# Revit family: CA-4_SWSI_ARR_1_CW_DBD
name_source: partatom
category: Mechanical Equipment
units: mm (PartAtom-declared; Revit-internal decimal feet)

## family parameters
Always vertical = Yes
Cut with Voids When Loaded = No
Part Type = Normal
Room Calculation Point = No
Round Connector Dimension = Use Radius
Shared = No
Work Plane-Based = No

## types (54) — shared parameters
0 = 0"
1" = 1"
1.5 = 1 1/2"
2" = 2"
2' = 24"
3" = 3"
4" = 4"
Manufacturer = Loren Cook Company
ONE EIGTH = 1/8"
Type Comments = Airfoil Centrifugal Blower Arrangement 1 Clockwise Down Blast Discharge
URL = www.lorencook.com

## per-type parameters (varying)
- 120_CA-4_SWSI_ARR_1_CW_DBD_CLASS_1: ((D-B)/2)-.125"=1 7/8"; ((K-B)/2)+B=12 17/32"; (D-B)/2=2"; (R-B)/2=1 1/8"; -(((D - B) / 2) - 1/8")=-1 7/8"; -(((K-B)/2)+L)=-6 11/32"; -(((K-B)/2)-.125")=-3 7/32"; -(ARR_2_L - ARR_2_K)=-17 5/8"; -ARR_1_J=-1 3/16"; 2ARR_1_J=2 3/8"; 2ARR_1_J+1"=3 3/8"; A=13 1/8"; ARR_1_G=9 3/16"; ARR_1_H=8 7/16"; ARR_1_J=1 3/16"; ARR_1_J/2=19/32"; ARR_1_K=30 13/16"; ARR_1_K-D=17 5/8"; ARR_1_M=1"; ARR_1_N=15 1/8"; ARR_1_U=34 13/16"; ARR_1_U-D=21 5/8"; ARR_1_V=4"; ARR_2_K=4"; ARR_2_L=21 5/8"; ARR_2_L-ARR_2_K=17 5/8"; B=9 3/16"; D=13 3/16"; D-((D-B)/2)=11 3/16"; E=10 3/4"; E+(INLET_RAD+1.5")=20"; E-(INLET_RAD+1.5")=3/4"; F=25 3/4"; F-E=15"; F/5=5 5/32"; G=22 3/4"; H=10 3/8"; INLET_DIA=16 1/4"; INLET_RAD=8 1/8"; INLET_RAD+1.5"=9 5/8"; INLET_RAD/2=4 1/16"; J=2"; K=15 7/8"; L=3"; M=18 7/8"; MOTOR_RAD=3 9/16"; Model=CA-4 SWSI ARR 1 CW DBD CLASS 1; O=11/16"; O/2=11/32"; P=5 23/32"; R=11 7/16"; S=7 1/2"
- 135_CA-4_SWSI_ARR_1_CW_DBD_CLASS_1: ((D-B)/2)-.125"=1 7/8"; ((K-B)/2)+B=13 21/32"; (D-B)/2=2"; (R-B)/2=1 1/8"; -(((D - B) / 2) - 1/8")=-1 7/8"; -(((K-B)/2)+L)=-6 11/32"; -(((K-B)/2)-.125")=-3 7/32"; -(ARR_2_L - ARR_2_K)=-17 5/8"; -ARR_1_J=-1 3/16"; 2ARR_1_J=2 3/8"; 2ARR_1_J+1"=3 3/8"; A=14 3/4"; ARR_1_G=9 15/16"; ARR_1_H=9 3/16"; ARR_1_J=1 3/16"; ARR_1_J/2=19/32"; ARR_1_K=31 15/16"; ARR_1_K-D=17 5/8"; ARR_1_M=1"; ARR_1_N=15 1/8"; ARR_1_U=35 15/16"; ARR_1_U-D=21 5/8"; ARR_1_V=4"; ARR_2_K=4"; ARR_2_L=21 5/8"; ARR_2_L-ARR_2_K=17 5/8"; B=10 5/16"; D=14 5/16"; D-((D-B)/2)=12 5/16"; E=12"; E+(INLET_RAD+1.5")=22"; E-(INLET_RAD+1.5")=1 1/4"; F=28 3/4"; F-E=16 3/4"; F/5=5 3/4"; G=25 1/2"; H=11 5/8"; INLET_DIA=17 3/4"; INLET_RAD=8 7/8"; INLET_RAD+1.5"=10 3/8"; INLET_RAD/2=4 7/16"; J=2"; K=17"; L=3"; M=20"; MOTOR_RAD=3 9/16"; Model=CA-4 SWSI ARR 1 CW DBD CLASS 1; O=11/16"; O/2=11/32"; P=6 9/32"; R=12 9/16"; S=8 1/2"
- 150_CA-4_SWSI_ARR_1_CW_DBD_CLASS_1: ((D-B)/2)-.125"=1 7/8"; ((K-B)/2)+B=14 25/32"; (D-B)/2=2"; (R-B)/2=1 1/8"; -(((D - B) / 2) - 1/8")=-1 7/8"; -(((K-B)/2)+L)=-6 11/32"; -(((K-B)/2)-.125")=-3 7/32"; -(ARR_2_L - ARR_2_K)=-17 5/8"; -ARR_1_J=-1 3/16"; 2ARR_1_J=2 3/8"; 2ARR_1_J+1"=3 3/8"; A=16 7/16"; ARR_1_G=10 11/16"; ARR_1_H=9 15/16"; ARR_1_J=1 3/16"; ARR_1_J/2=19/32"; ARR_1_K=33 1/16"; ARR_1_K-D=17 5/8"; ARR_1_M=1"; ARR_1_N=15 1/8"; ARR_1_U=37 1/16"; ARR_1_U-D=21 5/8"; ARR_1_V=4"; ARR_2_K=4"; ARR_2_L=21 5/8"; ARR_2_L-ARR_2_K=17 5/8"; B=11 7/16"; D=15 7/16"; D-((D-B)/2)=13 7/16"; E=13 1/4"; E+(INLET_RAD+1.5")=24"; E-(INLET_RAD+1.5")=1 3/4"; F=31 5/8"; F-E=18 3/8"; F/5=6 5/16"; G=28 1/8"; H=12 7/8"; INLET_DIA=19 1/4"; INLET_RAD=9 5/8"; INLET_RAD+1.5"=11 1/8"; INLET_RAD/2=4 13/16"; J=2"; K=18 1/8"; L=3"; M=21 1/8"; MOTOR_RAD=3 9/16"; Model=CA-4 SWSI ARR 1 CW DBD CLASS 1; O=11/16"; O/2=11/32"; P=6 27/32"; R=13 11/16"; S=9"
- 165_CA-4_SWSI_ARR_1_CW_DBD_CLASS_1: ((D-B)/2)-.125"=1 7/8"; ((K-B)/2)+B=15 31/32"; (D-B)/2=2"; (R-B)/2=1 1/8"; -(((D - B) / 2) - 1/8")=-1 7/8"; -(((K-B)/2)+L)=-7 11/32"; -(((K-B)/2)-.125")=-3 7/32"; -(ARR_2_L - ARR_2_K)=-17 5/8"; -ARR_1_J=-1 3/16"; 2ARR_1_J=2 3/8"; 2ARR_1_J+1"=3 3/8"; A=18 1/16"; ARR_1_G=11 11/16"; ARR_1_H=10 15/16"; ARR_1_J=1 3/16"; ARR_1_J/2=19/32"; ARR_1_K=34 1/4"; ARR_1_K-D=17 5/8"; ARR_1_M=1"; ARR_1_N=15 1/8"; ARR_1_U=38 1/4"; ARR_1_U-D=21 5/8"; ARR_1_V=4"; ARR_2_K=4"; ARR_2_L=21 5/8"; ARR_2_L-ARR_2_K=17 5/8"; B=12 5/8"; D=16 5/8"; D-((D-B)/2)=14 5/8"; E=14 3/8"; E+(INLET_RAD+1.5")=26 3/8"; E-(INLET_RAD+1.5")=2 1/8"; F=34 3/8"; F-E=20"; F/5=6 7/8"; G=30 7/8"; H=14 1/4"; INLET_DIA=21 1/4"; INLET_RAD=10 5/8"; INLET_RAD+1.5"=12 1/8"; INLET_RAD/2=5 5/16"; J=2"; K=19 5/16"; L=4"; M=23 15/16"; MOTOR_RAD=3 9/16"; Model=CA-4 SWSI ARR 1 CW DBD CLASS 1; O=11/16"; O/2=11/32"; P=7 7/16"; R=14 7/8"; S=10"
- 180_CA-4_SWSI_ARR_1_CW_DBD_CLASS_1: ((D-B)/2)-.125"=1 7/8"; ((K-B)/2)+B=17 3/32"; (D-B)/2=2"; (R-B)/2=1 1/8"; -(((D - B) / 2) - 1/8")=-1 7/8"; -(((K-B)/2)+L)=-7 27/32"; -(((K-B)/2)-.125")=-3 7/32"; -(ARR_2_L - ARR_2_K)=-20 1/8"; -ARR_1_J=-1 3/16"; 2ARR_1_J=2 3/8"; 2ARR_1_J+1"=3 3/8"; A=19 11/16"; ARR_1_G=12 7/16"; ARR_1_H=11 11/16"; ARR_1_J=1 3/16"; ARR_1_J/2=19/32"; ARR_1_K=37 7/8"; ARR_1_K-D=20 1/8"; ARR_1_M=1"; ARR_1_N=17 5/8"; ARR_1_U=42 1/8"; ARR_1_U-D=24 3/8"; ARR_1_V=4 1/4"; ARR_2_K=4 1/4"; ARR_2_L=24 3/8"; ARR_2_L-ARR_2_K=20 1/8"; B=13 3/4"; D=17 3/4"; D-((D-B)/2)=15 3/4"; E=15 5/8"; E+(INLET_RAD+1.5")=28 3/8"; E-(INLET_RAD+1.5")=2 5/8"; F=37 1/8"; F-E=21 1/2"; F/5=7 7/16"; G=33 5/8"; H=15 1/2"; INLET_DIA=22 3/4"; INLET_RAD=11 3/8"; INLET_RAD+1.5"=12 7/8"; INLET_RAD/2=5 11/16"; J=2"; K=20 7/16"; L=4 1/2"; M=24 15/16"; MOTOR_RAD=3 9/16"; Model=CA-4 SWSI ARR 1 CW DBD CLASS 1; O=11/16"; O/2=11/32"; P=8"; R=16"; S=11"
- 195_CA-4_SWSI_ARR_1_CW_DBD_CLASS_1: ((D-B)/2)-.125"=1 7/8"; ((K-B)/2)+B=18 13/16"; (D-B)/2=2"; (R-B)/2=1 1/8"; -(((D - B) / 2) - 1/8")=-1 7/8"; -(((K-B)/2)+L)=-8 3/8"; -(((K-B)/2)-.125")=-3 3/4"; -(ARR_2_L - ARR_2_K)=-20 1/8"; -ARR_1_J=-1 3/16"; 2ARR_1_J=2 3/8"; 2ARR_1_J+1"=3 3/8"; A=21 5/16"; ARR_1_G=13 3/16"; ARR_1_H=12 7/16"; ARR_1_J=1 3/16"; ARR_1_J/2=19/32"; ARR_1_K=39 1/16"; ARR_1_K-D=20 1/8"; ARR_1_M=1"; ARR_1_N=17 5/8"; ARR_1_U=43 5/16"; ARR_1_U-D=24 3/8"; ARR_1_V=4 1/4"; ARR_2_K=4 1/4"; ARR_2_L=24 3/8"; ARR_2_L-ARR_2_K=20 1/8"; B=14 15/16"; D=18 15/16"; D-((D-B)/2)=16 15/16"; E=16 3/4"; E+(INLET_RAD+1.5")=30 3/8"; E-(INLET_RAD+1.5")=3 1/8"; F=40"; F-E=23 1/4"; F/5=8"; G=36 1/4"; H=16 3/4"; INLET_DIA=24 1/4"; INLET_RAD=12 1/8"; INLET_RAD+1.5"=13 5/8"; INLET_RAD/2=6 1/16"; J=2"; K=22 11/16"; L=4 1/2"; M=27 3/16"; MOTOR_RAD=3 9/16"; Model=CA-4 SWSI ARR 1 CW DBD CLASS 1; O=11/16"; O/2=11/32"; P=8 19/32"; R=17 3/16"; S=11 1/2"
- 210_CA-4_SWSI_ARR_1_CW_DBD_CLASS_1: ((D-B)/2)-.125"=1 7/8"; ((K-B)/2)+B=19 15/16"; (D-B)/2=2"; (R-B)/2=1 1/8"; -(((D - B) / 2) - 1/8")=-1 7/8"; -(((K-B)/2)+L)=-8 7/8"; -(((K-B)/2)-.125")=-3 3/4"; -(ARR_2_L - ARR_2_K)=-23 1/8"; -ARR_1_J=-1 7/16"; 2ARR_1_J=2 7/8"; 2ARR_1_J+1"=3 7/8"; A=23"; ARR_1_G=14 1/16"; ARR_1_H=13 5/16"; ARR_1_J=1 7/16"; ARR_1_J/2=23/32"; ARR_1_K=42 3/16"; ARR_1_K-D=22 1/8"; ARR_1_M=1"; ARR_1_N=19 9/16"; ARR_1_U=46 7/16"; ARR_1_U-D=26 3/8"; ARR_1_V=4 1/4"; ARR_2_K=4 1/4"; ARR_2_L=27 3/8"; ARR_2_L-ARR_2_K=23 1/8"; B=16 1/16"; D=20 1/16"; D-((D-B)/2)=18 1/16"; E=18"; E+(INLET_RAD+1.5")=32 5/8"; E-(INLET_RAD+1.5")=3 5/8"; F=42 7/8"; F-E=24 7/8"; F/5=8 9/16"; G=39 1/8"; H=18 1/8"; INLET_DIA=26"; INLET_RAD=13"; INLET_RAD+1.5"=14 1/2"; INLET_RAD/2=6 1/2"; J=2"; K=23 13/16"; L=5"; M=28 13/16"; MOTOR_RAD=4 5/16"; Model=CA-4 SWSI ARR 1 CW DBD CLASS 1; O=13/16"; O/2=13/32"; P=9 5/32"; R=18 5/16"; S=12"
- 225_CA-4_SWSI_ARR_1_CW_DBD_CLASS_1: ((D-B)/2)-.125"=1 7/8"; ((K-B)/2)+B=21 1/16"; (D-B)/2=2"; (R-B)/2=1 1/8"; -(((D - B) / 2) - 1/8")=-1 7/8"; -(((K-B)/2)+L)=-8 7/8"; -(((K-B)/2)-.125")=-3 3/4"; -(ARR_2_L - ARR_2_K)=-23 1/8"; -ARR_1_J=-1 7/16"; 2ARR_1_J=2 7/8"; 2ARR_1_J+1"=3 7/8"; A=24 5/8"; ARR_1_G=14 13/16"; ARR_1_H=14 1/16"; ARR_1_J=1 7/16"; ARR_1_J/2=23/32"; ARR_1_K=43 5/16"; ARR_1_K-D=22 1/8"; ARR_1_M=1"; ARR_1_N=19 9/16"; ARR_1_U=47 9/16"; ARR_1_U-D=26 3/8"; ARR_1_V=4 1/4"; ARR_2_K=4 1/4"; ARR_2_L=27 3/8"; ARR_2_L-ARR_2_K=23 1/8"; B=17 3/16"; D=21 3/16"; D-((D-B)/2)=19 3/16"; E=19 1/4"; E+(INLET_RAD+1.5")=34 5/8"; E-(INLET_RAD+1.5")=4 1/8"; F=45 3/4"; F-E=26 1/2"; F/5=9 5/32"; G=41 3/4"; H=19 3/8"; INLET_DIA=27 1/2"; INLET_RAD=13 3/4"; INLET_RAD+1.5"=15 1/4"; INLET_RAD/2=6 7/8"; J=2"; K=24 15/16"; L=5"; M=29 15/16"; MOTOR_RAD=4 5/16"; Model=CA-4 SWSI ARR 1 CW DBD CLASS 1; O=13/16"; O/2=13/32"; P=9 23/32"; R=19 7/16"; S=12 1/2"
- 245_CA-4_SWSI_ARR_1_CW_DBD_CLASS_1: ((D-B)/2)-.125"=1 7/8"; ((K-B)/2)+B=22 5/8"; (D-B)/2=2"; (R-B)/2=1 1/8"; -(((D - B) / 2) - 1/8")=-1 7/8"; -(((K-B)/2)+L)=-9 3/8"; -(((K-B)/2)-.125")=-3 3/4"; -(ARR_2_L - ARR_2_K)=-22 9/16"; -ARR_1_J=-1 11/16"; 2ARR_1_J=3 3/8"; 2ARR_1_J+1"=4 3/8"; A=26 13/16"; ARR_1_G=15 13/16"; ARR_1_H=15 1/16"; ARR_1_J=1 11/16"; ARR_1_J/2=27/32"; ARR_1_K=45 3/8"; ARR_1_K-D=22 5/8"; ARR_1_M=1"; ARR_1_N=20 1/8"; ARR_1_U=50 9/16"; ARR_1_U-D=27 13/16"; ARR_1_V=5 1/4"; ARR_2_K=5 1/4"; ARR_2_L=27 13/16"; ARR_2_L-ARR_2_K=22 9/16"; B=18 3/4"; D=22 3/4"; D-((D-B)/2)=20 3/4"; E=20 7/8"; E+(INLET_RAD+1.5")=37 3/8"; E-(INLET_RAD+1.5")=4 7/8"; F=49 1/2"; F-E=28 5/8"; F/5=9 29/32"; G=45 3/8"; H=21 1/8"; INLET_DIA=29 1/2"; INLET_RAD=14 3/4"; INLET_RAD+1.5"=16 1/4"; INLET_RAD/2=7 3/8"; J=2"; K=26 1/2"; L=5 1/2"; M=32"; MOTOR_RAD=5 1/16"; Model=CA-4 SWSI ARR 1 CW DBD CLASS 1; O=13/16"; O/2=13/32"; P=10 1/2"; R=21"; S=13 1/2"
- 270_CA-4_SWSI_ARR_1_CW_DBD_CLASS_1: ((D-B)/2)-.125"=1 7/8"; ((K-B)/2)+B=24 1/2"; (D-B)/2=2"; (R-B)/2=1 1/8"; -(((D - B) / 2) - 1/8")=-1 7/8"; -(((K-B)/2)+L)=-9 7/8"; -(((K-B)/2)-.125")=-3 3/4"; -(ARR_2_L - ARR_2_K)=-22 9/16"; -ARR_1_J=-1 11/16"; 2ARR_1_J=3 3/8"; 2ARR_1_J+1"=4 3/8"; A=29 9/16"; ARR_1_G=17 3/16"; ARR_1_H=16 7/16"; ARR_1_J=1 11/16"; ARR_1_J/2=27/32"; ARR_1_K=47 1/4"; ARR_1_K-D=22 5/8"; ARR_1_M=1"; ARR_1_N=20 1/8"; ARR_1_U=52 7/16"; ARR_1_U-D=27 13/16"; ARR_1_V=5 1/4"; ARR_2_K=5 1/4"; ARR_2_L=27 13/16"; ARR_2_L-ARR_2_K=22 9/16"; B=20 5/8"; D=24 5/8"; D-((D-B)/2)=22 5/8"; E=23 3/8"; E+(INLET_RAD+1.5")=40 3/4"; E-(INLET_RAD+1.5")=5 3/4"; F=54 3/4"; F-E=31 3/8"; F/5=10 15/16"; G=49 7/8"; H=23 1/4"; INLET_DIA=32"; INLET_RAD=16"; INLET_RAD+1.5"=17 1/2"; INLET_RAD/2=8"; J=2"; K=28 3/8"; L=6"; M=34 3/8"; MOTOR_RAD=5 1/16"; Model=CA-4 SWSI ARR 1 CW DBD CLASS 1; O=13/16"; O/2=13/32"; P=11 7/16"; R=22 7/8"; S=15"
- 300_CA-4_SWSI_ARR_1_CW_DBD_CLASS_1: ((D-B)/2)-.125"=1 7/8"; ((K-B)/2)+B=26 13/16"; (D-B)/2=2"; (R-B)/2=1 1/8"; -(((D - B) / 2) - 1/8")=-1 7/8"; -(((K-B)/2)+L)=-10 3/8"; -(((K-B)/2)-.125")=-3 3/4"; -(ARR_2_L - ARR_2_K)=-24 7/8"; -ARR_1_J=-1 15/16"; 2ARR_1_J=3 7/8"; 2ARR_1_J+1"=4 7/8"; A=32 13/16"; ARR_1_G=18 11/16"; ARR_1_H=17 15/16"; ARR_1_J=1 15/16"; ARR_1_J/2=31/32"; ARR_1_K=51 13/16"; ARR_1_K-D=24 7/8"; ARR_1_M=1"; ARR_1_N=22 3/8"; ARR_1_U=57 11/16"; ARR_1_U-D=30 3/4"; ARR_1_V=5 7/8"; ARR_2_K=5 7/8"; ARR_2_L=30 3/4"; ARR_2_L-ARR_2_K=24 7/8"; B=22 15/16"; D=26 15/16"; D-((D-B)/2)=24 15/16"; E=25 3/8"; E+(INLET_RAD+1.5")=44 7/8"; E-(INLET_RAD+1.5")=6 7/8"; F=60"; F-E=34 5/8"; F/5=12"; G=55 3/8"; H=25 7/8"; INLET_DIA=35"; INLET_RAD=17 1/2"; INLET_RAD+1.5"=19"; INLET_RAD/2=8 3/4"; J=2"; K=30 11/16"; L=6 1/2"; M=37 3/16"; MOTOR_RAD=5 13/16"; Model=CA-4 SWSI ARR 1 CW DBD CLASS 1; O=13/16"; O/2=13/32"; P=12 19/32"; R=25 3/16"; S=16 1/2"
- 330_CA-4_SWSI_ARR_1_CW_DBD_CLASS_1: ((D-B)/2)-.125"=1 7/8"; ((K-B)/2)+B=29 1/8"; (D-B)/2=2"; (R-B)/2=1 1/8"; -(((D - B) / 2) - 1/8")=-1 7/8"; -(((K-B)/2)+L)=-10 7/8"; -(((K-B)/2)-.125")=-3 3/4"; -(ARR_2_L - ARR_2_K)=-24 7/8"; -ARR_1_J=-1 15/16"; 2ARR_1_J=3 7/8"; 2ARR_1_J+1"=4 7/8"; A=36 1/8"; ARR_1_G=20 3/16"; ARR_1_H=19 7/16"; ARR_1_J=1 15/16"; ARR_1_J/2=31/32"; ARR_1_K=54 1/8"; ARR_1_K-D=24 7/8"; ARR_1_M=1"; ARR_1_N=22 3/8"; ARR_1_U=60"; ARR_1_U-D=30 3/4"; ARR_1_V=5 7/8"; ARR_2_K=5 7/8"; ARR_2_L=30 3/4"; ARR_2_L-ARR_2_K=24 7/8"; B=25 1/4"; D=29 1/4"; D-((D-B)/2)=27 1/4"; E=27 7/8"; E+(INLET_RAD+1.5")=48 7/8"; E-(INLET_RAD+1.5")=7 7/8"; F=65 3/4"; F-E=37 7/8"; F/5=13 5/32"; G=60 3/4"; H=28 3/8"; INLET_DIA=38"; INLET_RAD=19"; INLET_RAD+1.5"=20 1/2"; INLET_RAD/2=9 1/2"; J=2"; K=33"; L=7"; M=40"; MOTOR_RAD=5 13/16"; Model=CA-4 SWSI ARR 1 CW DBD CLASS 1; O=13/16"; O/2=13/32"; P=13 3/4"; R=27 1/2"; S=18"
- 365_CA-4_SWSI_ARR_1_CW_DBD_CLASS_1: ((D-B)/2)-.125"=1 7/8"; ((K-B)/2)+B=31 3/4"; (D-B)/2=2"; (R-B)/2=1 1/8"; -(((D - B) / 2) - 1/8")=-1 7/8"; -(((K-B)/2)+L)=-11 3/8"; -(((K-B)/2)-.125")=-3 3/4"; -(ARR_2_L - ARR_2_K)=-27 1/8"; -ARR_1_J=-2 3/16"; 2ARR_1_J=4 3/8"; 2ARR_1_J+1"=5 3/8"; A=39 15/16"; ARR_1_G=22 7/16"; ARR_1_H=21 11/16"; ARR_1_J=2 3/16"; ARR_1_J/2=1 3/32"; ARR_1_K=59"; ARR_1_K-D=27 1/8"; ARR_1_M=1"; ARR_1_N=24 5/8"; ARR_1_U=64 7/8"; ARR_1_U-D=33"; ARR_1_V=5 7/8"; ARR_2_K=5 7/8"; ARR_2_L=33"; ARR_2_L-ARR_2_K=27 1/8"; B=27 7/8"; D=31 7/8"; D-((D-B)/2)=29 7/8"; E=30 5/8"; E+(INLET_RAD+1.5")=53 5/8"; E-(INLET_RAD+1.5")=9 1/8"; F=72 3/8"; F-E=41 3/4"; F/5=14 15/32"; G=67"; H=31 3/8"; INLET_DIA=41 1/2"; INLET_RAD=20 3/4"; INLET_RAD+1.5"=22 1/4"; INLET_RAD/2=10 3/8"; J=2"; K=35 5/8"; L=7 1/2"; M=43 1/8"; MOTOR_RAD=6 9/16"; Model=CA-4 SWSI ARR 1 CW DBD CLASS 1; O=13/16"; O/2=13/32"; P=15 1/16"; R=30 1/8"; S=20"
- 402_CA-4_SWSI_ARR_1_CW_DBD_CLASS_1: ((D-B)/2)-.125"=2 7/8"; ((K-B)/2)+B=34 11/16"; (D-B)/2=3"; (R-B)/2=1 3/4"; -(((D - B) / 2) - 1/8")=-2 7/8"; -(((K-B)/2)+L)=-11 15/16"; -(((K-B)/2)-.125")=-3 13/16"; -(ARR_2_L - ARR_2_K)=-25 7/16"; -ARR_1_J=-2 3/16"; 2ARR_1_J=4 3/8"; 2ARR_1_J+1"=5 3/8"; A=44 1/16"; ARR_1_G=24 3/8"; ARR_1_H=22 3/8"; ARR_1_J=2 3/16"; ARR_1_J/2=1 3/32"; ARR_1_K=62 15/16"; ARR_1_K-D=26 3/16"; ARR_1_M=1 1/4"; ARR_1_N=23 13/16"; ARR_1_U=68 1/16"; ARR_1_U-D=31 5/16"; ARR_1_V=5 7/8"; ARR_2_K=5 7/8"; ARR_2_L=31 5/16"; ARR_2_L-ARR_2_K=25 7/16"; B=30 3/4"; D=36 3/4"; D-((D-B)/2)=33 3/4"; E=33 5/8"; E+(INLET_RAD+1.5")=58 3/4"; E-(INLET_RAD+1.5")=10 1/2"; F=80 3/8"; F-E=46 3/4"; F/5=16 1/16"; G=73 7/8"; H=34 5/8"; INLET_DIA=45 1/4"; INLET_RAD=22 5/8"; INLET_RAD+1.5"=24 1/8"; INLET_RAD/2=11 5/16"; J=3"; K=38 5/8"; L=8"; M=46 5/8"; MOTOR_RAD=6 9/16"; Model=CA-4 SWSI ARR 1 CW DBD CLASS 1; O=1 1/16"; O/2=17/32"; P=17 1/8"; R=34 1/4"; S=22"
- 445_CA-4_SWSI_ARR_1_CW_DBD_CLASS_1: ((D-B)/2)-.125"=2 7/8"; ((K-B)/2)+B=37 15/16"; (D-B)/2=3"; (R-B)/2=1 3/4"; -(((D - B) / 2) - 1/8")=-2 7/8"; -(((K-B)/2)+L)=-12 7/16"; -(((K-B)/2)-.125")=-3 13/16"; -(ARR_2_L - ARR_2_K)=-26 11/16"; -ARR_1_J=-2 7/16"; 2ARR_1_J=4 7/8"; 2ARR_1_J+1"=5 7/8"; A=48 11/16"; ARR_1_G=26 1/2"; ARR_1_H=25 1/2"; ARR_1_J=2 7/16"; ARR_1_J/2=1 7/32"; ARR_1_K=66 15/16"; ARR_1_K-D=26 15/16"; ARR_1_M=1 1/4"; ARR_1_N=24 9/16"; ARR_1_U=73 1/16"; ARR_1_U-D=33 1/16"; ARR_1_V=6 3/8"; ARR_2_K=6 3/8"; ARR_2_L=33 1/16"; ARR_2_L-ARR_2_K=26 11/16"; B=34"; D=40"; D-((D-B)/2)=37"; E=37 1/8"; E+(INLET_RAD+1.5")=64 1/2"; E-(INLET_RAD+1.5")=12"; F=88 1/2"; F-E=51 3/8"; F/5=17 11/16"; G=81 1/2"; H=38 1/4"; INLET_DIA=49 1/2"; INLET_RAD=24 3/4"; INLET_RAD+1.5"=26 1/4"; INLET_RAD/2=12 3/8"; J=3"; K=41 7/8"; L=8 1/2"; M=50 3/8"; MOTOR_RAD=7 5/16"; Model=CA-4 SWSI ARR 1 CW DBD CLASS 1; O=1 1/16"; O/2=17/32"; P=18 3/4"; R=37 1/2"; S=24"
- 490_CA-4_SWSI_ARR_1_CW_DBD_CLASS_1: ((D-B)/2)-.125"=2 7/8"; ((K-B)/2)+B=41 7/8"; (D-B)/2=3"; (R-B)/2=1 3/4"; -(((D - B) / 2) - 1/8")=-2 7/8"; -(((K-B)/2)+L)=-13 7/16"; -(((K-B)/2)-.125")=-4 5/16"; -(ARR_2_L - ARR_2_K)=-26 11/16"; -ARR_1_J=-2 7/16"; 2ARR_1_J=4 7/8"; 2ARR_1_J+1"=5 7/8"; A=53 5/8"; ARR_1_G=29 1/4"; ARR_1_H=28 1/4"; ARR_1_J=2 7/16"; ARR_1_J/2=1 7/32"; ARR_1_K=70 3/8"; ARR_1_K-D=26 15/16"; ARR_1_M=1 1/4"; ARR_1_N=24 9/16"; ARR_1_U=76 1/2"; ARR_1_U-D=33 1/16"; ARR_1_V=6 3/8"; ARR_2_K=6 3/8"; ARR_2_L=33 1/16"; ARR_2_L-ARR_2_K=26 11/16"; B=37 7/16"; D=43 7/16"; D-((D-B)/2)=40 7/16"; E=40 3/4"; E+(INLET_RAD+1.5")=71 1/4"; E-(INLET_RAD+1.5")=13 1/4"; F=97"; F-E=56 1/4"; F/5=19 13/32"; G=89 3/4"; H=42 1/4"; INLET_DIA=55"; INLET_RAD=27 1/2"; INLET_RAD+1.5"=29"; INLET_RAD/2=13 3/4"; J=3"; K=46 5/16"; L=9"; M=55 5/16"; MOTOR_RAD=7 5/16"; Model=CA-4 SWSI ARR 1 CW DBD CLASS 1; O=1 1/16"; O/2=17/32"; P=20 15/32"; R=40 15/16"; S=26 1/2"
- 540_CA-4_SWSI_ARR_1_CW_DBD_CLASS_1: ((D-B)/2)-.125"=2 7/8"; ((K-B)/2)+B=46 11/16"; (D-B)/2=3"; (R-B)/2=1 3/4"; -(((D - B) / 2) - 1/8")=-2 7/8"; -(((K-B)/2)+L)=-14 15/16"; -(((K-B)/2)-.125")=-5 5/16"; -(ARR_2_L - ARR_2_K)=-26 7/8"; -ARR_1_J=-2 15/16"; 2ARR_1_J=5 7/8"; 2ARR_1_J+1"=6 7/8"; A=59 1/16"; ARR_1_G=31 3/4"; ARR_1_H=30 3/4"; ARR_1_J=2 15/16"; ARR_1_J/2=1 15/32"; ARR_1_K=74 1/4"; ARR_1_K-D=27"; ARR_1_M=1 1/4"; ARR_1_N=24 9/16"; ARR_1_U=81 5/8"; ARR_1_U-D=34 3/8"; ARR_1_V=7 1/2"; ARR_2_K=7 1/2"; ARR_2_L=34 3/8"; ARR_2_L-ARR_2_K=26 7/8"; B=41 1/4"; D=47 1/4"; D-((D-B)/2)=44 1/4"; E=44 7/8"; E+(INLET_RAD+1.5")=78"; E-(INLET_RAD+1.5")=15"; F=106 5/8"; F-E=61 3/4"; F/5=21 5/16"; G=98 3/4"; H=46 1/2"; INLET_DIA=60"; INLET_RAD=30"; INLET_RAD+1.5"=31 1/2"; INLET_RAD/2=15"; J=3"; K=52 1/8"; L=9 1/2"; M=61 5/8"; MOTOR_RAD=8 13/16"; Model=CA-4 SWSI ARR 1 CW DBD CLASS 1; O=1 1/16"; O/2=17/32"; P=22 3/8"; R=44 3/4"; S=29"
- 600_CA-4_SWSI_ARR_1_CW_DBD_CLASS_1: ((D-B)/2)-.125"=2 7/8"; ((K-B)/2)+B=51 1/4"; (D-B)/2=3"; (R-B)/2=1 3/4"; -(((D - B) / 2) - 1/8")=-2 7/8"; -(((K-B)/2)+L)=-15 7/16"; -(((K-B)/2)-.125")=-5 5/16"; -(ARR_2_L - ARR_2_K)=-26 7/8"; -ARR_1_J=-2 15/16"; 2ARR_1_J=5 7/8"; 2ARR_1_J+1"=6 7/8"; A=65 5/8"; ARR_1_G=34 3/4"; ARR_1_H=33 3/4"; ARR_1_J=2 15/16"; ARR_1_J/2=1 15/32"; ARR_1_K=78 13/16"; ARR_1_K-D=27"; ARR_1_M=1 1/4"; ARR_1_N=24 9/16"; ARR_1_U=86 3/16"; ARR_1_U-D=34 3/8"; ARR_1_V=7 1/2"; ARR_2_K=7 1/2"; ARR_2_L=34 3/8"; ARR_2_L-ARR_2_K=26 7/8"; B=45 13/16"; D=51 13/16"; D-((D-B)/2)=48 13/16"; E=49 3/4"; E+(INLET_RAD+1.5")=86 1/8"; E-(INLET_RAD+1.5")=17 1/8"; F=118"; F-E=68 1/4"; F/5=23 19/32"; G=109 5/8"; H=51 5/8"; INLET_DIA=66"; INLET_RAD=33"; INLET_RAD+1.5"=34 1/2"; INLET_RAD/2=16 1/2"; J=3"; K=56 11/16"; L=10"; M=66 11/16"; MOTOR_RAD=8 13/16"; Model=CA-4 SWSI ARR 1 CW DBD CLASS 1; O=1 1/16"; O/2=17/32"; P=24 21/32"; R=49 5/16"; S=32"
- 120_CA-4_SWSI_ARR_1_CW_DBD_CLASS_2: ((D-B)/2)-.125"=1 7/8"; ((K-B)/2)+B=12 17/32"; (D-B)/2=2"; (R-B)/2=1 1/8"; -(((D - B) / 2) - 1/8")=-1 7/8"; -(((K-B)/2)+L)=-6 11/32"; -(((K-B)/2)-.125")=-3 7/32"; -(ARR_2_L - ARR_2_K)=-17 5/8"; -ARR_1_J=-1 7/16"; 2ARR_1_J=2 7/8"; 2ARR_1_J+1"=3 7/8"; A=13 1/8"; ARR_1_G=9 3/16"; ARR_1_H=8 7/16"; ARR_1_J=1 7/16"; ARR_1_J/2=23/32"; ARR_1_K=30 13/16"; ARR_1_K-D=17 5/8"; ARR_1_M=1"; ARR_1_N=15 1/8"; ARR_1_U=34 13/16"; ARR_1_U-D=21 5/8"; ARR_1_V=4"; ARR_2_K=4"; ARR_2_L=21 5/8"; ARR_2_L-ARR_2_K=17 5/8"; B=9 3/16"; D=13 3/16"; D-((D-B)/2)=11 3/16"; E=10 3/4"; E+(INLET_RAD+1.5")=20"; E-(INLET_RAD+1.5")=3/4"; F=25 3/4"; F-E=15"; F/5=5 5/32"; G=22 3/4"; H=10 3/8"; INLET_DIA=16 1/4"; INLET_RAD=8 1/8"; INLET_RAD+1.5"=9 5/8"; INLET_RAD/2=4 1/16"; J=2"; K=15 7/8"; L=3"; M=18 7/8"; MOTOR_RAD=4 5/16"; Model=CA-4 SWSI ARR 1 CW DBD CLASS 2; O=11/16"; O/2=11/32"; P=5 23/32"; R=11 7/16"; S=7 1/2"
- 120_CA-4_SWSI_ARR_1_CW_DBD_CLASS_3: ((D-B)/2)-.125"=1 7/8"; ((K-B)/2)+B=12 17/32"; (D-B)/2=2"; (R-B)/2=1 1/8"; -(((D - B) / 2) - 1/8")=-1 7/8"; -(((K-B)/2)+L)=-6 11/32"; -(((K-B)/2)-.125")=-3 7/32"; -(ARR_2_L - ARR_2_K)=-17 5/8"; -ARR_1_J=-1 7/16"; 2ARR_1_J=2 7/8"; 2ARR_1_J+1"=3 7/8"; A=13 1/8"; ARR_1_G=9 3/16"; ARR_1_H=8 7/16"; ARR_1_J=1 7/16"; ARR_1_J/2=23/32"; ARR_1_K=30 13/16"; ARR_1_K-D=17 5/8"; ARR_1_M=1"; ARR_1_N=15 1/8"; ARR_1_U=34 13/16"; ARR_1_U-D=21 5/8"; ARR_1_V=4"; ARR_2_K=4"; ARR_2_L=21 5/8"; ARR_2_L-ARR_2_K=17 5/8"; B=9 3/16"; D=13 3/16"; D-((D-B)/2)=11 3/16"; E=10 3/4"; E+(INLET_RAD+1.5")=20"; E-(INLET_RAD+1.5")=3/4"; F=25 3/4"; F-E=15"; F/5=5 5/32"; G=22 3/4"; H=10 3/8"; INLET_DIA=16 1/4"; INLET_RAD=8 1/8"; INLET_RAD+1.5"=9 5/8"; INLET_RAD/2=4 1/16"; J=2"; K=15 7/8"; L=3"; M=18 7/8"; MOTOR_RAD=4 5/16"; Model=CA-4 SWSI ARR 1 CW DBD CLASS 3; O=11/16"; O/2=11/32"; P=5 23/32"; R=11 7/16"; S=7 1/2"
- 135_CA-4_SWSI_ARR_1_CW_DBD_CLASS_2: ((D-B)/2)-.125"=1 7/8"; ((K-B)/2)+B=13 21/32"; (D-B)/2=2"; (R-B)/2=1 1/8"; -(((D - B) / 2) - 1/8")=-1 7/8"; -(((K-B)/2)+L)=-6 11/32"; -(((K-B)/2)-.125")=-3 7/32"; -(ARR_2_L - ARR_2_K)=-17 5/8"; -ARR_1_J=-1 7/16"; 2ARR_1_J=2 7/8"; 2ARR_1_J+1"=3 7/8"; A=14 3/4"; ARR_1_G=9 15/16"; ARR_1_H=9 3/16"; ARR_1_J=1 7/16"; ARR_1_J/2=23/32"; ARR_1_K=31 15/16"; ARR_1_K-D=17 5/8"; ARR_1_M=1"; ARR_1_N=15 1/8"; ARR_1_U=35 15/16"; ARR_1_U-D=21 5/8"; ARR_1_V=4"; ARR_2_K=4"; ARR_2_L=21 5/8"; ARR_2_L-ARR_2_K=17 5/8"; B=10 5/16"; D=14 5/16"; D-((D-B)/2)=12 5/16"; E=12"; E+(INLET_RAD+1.5")=22"; E-(INLET_RAD+1.5")=1 1/4"; F=28 3/4"; F-E=16 3/4"; F/5=5 3/4"; G=25 1/2"; H=11 5/8"; INLET_DIA=17 3/4"; INLET_RAD=8 7/8"; INLET_RAD+1.5"=10 3/8"; INLET_RAD/2=4 7/16"; J=2"; K=17"; L=3"; M=20"; MOTOR_RAD=4 5/16"; Model=CA-4 SWSI ARR 1 CW DBD CLASS 2; O=11/16"; O/2=11/32"; P=6 9/32"; R=12 9/16"; S=8 1/2"
- 135_CA-4_SWSI_ARR_1_CW_DBD_CLASS_3: ((D-B)/2)-.125"=1 7/8"; ((K-B)/2)+B=13 21/32"; (D-B)/2=2"; (R-B)/2=1 1/8"; -(((D - B) / 2) - 1/8")=-1 7/8"; -(((K-B)/2)+L)=-6 11/32"; -(((K-B)/2)-.125")=-3 7/32"; -(ARR_2_L - ARR_2_K)=-17 5/8"; -ARR_1_J=-1 7/16"; 2ARR_1_J=2 7/8"; 2ARR_1_J+1"=3 7/8"; A=14 3/4"; ARR_1_G=9 15/16"; ARR_1_H=9 3/16"; ARR_1_J=1 7/16"; ARR_1_J/2=23/32"; ARR_1_K=31 15/16"; ARR_1_K-D=17 5/8"; ARR_1_M=1"; ARR_1_N=15 1/8"; ARR_1_U=35 15/16"; ARR_1_U-D=21 5/8"; ARR_1_V=4"; ARR_2_K=4"; ARR_2_L=21 5/8"; ARR_2_L-ARR_2_K=17 5/8"; B=10 5/16"; D=14 5/16"; D-((D-B)/2)=12 5/16"; E=12"; E+(INLET_RAD+1.5")=22"; E-(INLET_RAD+1.5")=1 1/4"; F=28 3/4"; F-E=16 3/4"; F/5=5 3/4"; G=25 1/2"; H=11 5/8"; INLET_DIA=17 3/4"; INLET_RAD=8 7/8"; INLET_RAD+1.5"=10 3/8"; INLET_RAD/2=4 7/16"; J=2"; K=17"; L=3"; M=20"; MOTOR_RAD=4 5/16"; Model=CA-4 SWSI ARR 1 CW DBD CLASS 3; O=11/16"; O/2=11/32"; P=6 9/32"; R=12 9/16"; S=8 1/2"
- 150_CA-4_SWSI_ARR_1_CW_DBD_CLASS_2: ((D-B)/2)-.125"=1 7/8"; ((K-B)/2)+B=14 25/32"; (D-B)/2=2"; (R-B)/2=1 1/8"; -(((D - B) / 2) - 1/8")=-1 7/8"; -(((K-B)/2)+L)=-6 11/32"; -(((K-B)/2)-.125")=-3 7/32"; -(ARR_2_L - ARR_2_K)=-17 5/8"; -ARR_1_J=-1 7/16"; 2ARR_1_J=2 7/8"; 2ARR_1_J+1"=3 7/8"; A=16 7/16"; ARR_1_G=10 11/16"; ARR_1_H=9 15/16"; ARR_1_J=1 7/16"; ARR_1_J/2=23/32"; ARR_1_K=33 1/16"; ARR_1_K-D=17 5/8"; ARR_1_M=1"; ARR_1_N=15 1/8"; ARR_1_U=37 1/16"; ARR_1_U-D=21 5/8"; ARR_1_V=4"; ARR_2_K=4"; ARR_2_L=21 5/8"; ARR_2_L-ARR_2_K=17 5/8"; B=11 7/16"; D=15 7/16"; D-((D-B)/2)=13 7/16"; E=13 1/4"; E+(INLET_RAD+1.5")=24"; E-(INLET_RAD+1.5")=1 3/4"; F=31 5/8"; F-E=18 3/8"; F/5=6 5/16"; G=28 1/8"; H=12 7/8"; INLET_DIA=19 1/4"; INLET_RAD=9 5/8"; INLET_RAD+1.5"=11 1/8"; INLET_RAD/2=4 13/16"; J=2"; K=18 1/8"; L=3"; M=21 1/8"; MOTOR_RAD=4 5/16"; Model=CA-4 SWSI ARR 1 CW DBD CLASS 2; O=11/16"; O/2=11/32"; P=6 27/32"; R=13 11/16"; S=9"
- 150_CA-4_SWSI_ARR_1_CW_DBD_CLASS_3: ((D-B)/2)-.125"=1 7/8"; ((K-B)/2)+B=14 25/32"; (D-B)/2=2"; (R-B)/2=1 1/8"; -(((D - B) / 2) - 1/8")=-1 7/8"; -(((K-B)/2)+L)=-6 11/32"; -(((K-B)/2)-.125")=-3 7/32"; -(ARR_2_L - ARR_2_K)=-17 5/8"; -ARR_1_J=-1 7/16"; 2ARR_1_J=2 7/8"; 2ARR_1_J+1"=3 7/8"; A=16 7/16"; ARR_1_G=10 11/16"; ARR_1_H=9 15/16"; ARR_1_J=1 7/16"; ARR_1_J/2=23/32"; ARR_1_K=33 1/16"; ARR_1_K-D=17 5/8"; ARR_1_M=1"; ARR_1_N=15 1/8"; ARR_1_U=37 1/16"; ARR_1_U-D=21 5/8"; ARR_1_V=4"; ARR_2_K=4"; ARR_2_L=21 5/8"; ARR_2_L-ARR_2_K=17 5/8"; B=11 7/16"; D=15 7/16"; D-((D-B)/2)=13 7/16"; E=13 1/4"; E+(INLET_RAD+1.5")=24"; E-(INLET_RAD+1.5")=1 3/4"; F=31 5/8"; F-E=18 3/8"; F/5=6 5/16"; G=28 1/8"; H=12 7/8"; INLET_DIA=19 1/4"; INLET_RAD=9 5/8"; INLET_RAD+1.5"=11 1/8"; INLET_RAD/2=4 13/16"; J=2"; K=18 1/8"; L=3"; M=21 1/8"; MOTOR_RAD=4 5/16"; Model=CA-4 SWSI ARR 1 CW DBD CLASS 3; O=11/16"; O/2=11/32"; P=6 27/32"; R=13 11/16"; S=9"
- 165_CA-4_SWSI_ARR_1_CW_DBD_CLASS_2: ((D-B)/2)-.125"=1 7/8"; ((K-B)/2)+B=15 31/32"; (D-B)/2=2"; (R-B)/2=1 1/8"; -(((D - B) / 2) - 1/8")=-1 7/8"; -(((K-B)/2)+L)=-7 11/32"; -(((K-B)/2)-.125")=-3 7/32"; -(ARR_2_L - ARR_2_K)=-17 5/8"; -ARR_1_J=-1 7/16"; 2ARR_1_J=2 7/8"; 2ARR_1_J+1"=3 7/8"; A=18 1/16"; ARR_1_G=11 11/16"; ARR_1_H=10 15/16"; ARR_1_J=1 7/16"; ARR_1_J/2=23/32"; ARR_1_K=34 1/4"; ARR_1_K-D=17 5/8"; ARR_1_M=1"; ARR_1_N=15 1/8"; ARR_1_U=38 1/4"; ARR_1_U-D=21 5/8"; ARR_1_V=4"; ARR_2_K=4"; ARR_2_L=21 5/8"; ARR_2_L-ARR_2_K=17 5/8"; B=12 5/8"; D=16 5/8"; D-((D-B)/2)=14 5/8"; E=14 3/8"; E+(INLET_RAD+1.5")=26 3/8"; E-(INLET_RAD+1.5")=2 1/8"; F=34 3/8"; F-E=20"; F/5=6 7/8"; G=30 7/8"; H=14 1/4"; INLET_DIA=21 1/4"; INLET_RAD=10 5/8"; INLET_RAD+1.5"=12 1/8"; INLET_RAD/2=5 5/16"; J=2"; K=19 5/16"; L=4"; M=23 15/16"; MOTOR_RAD=4 5/16"; Model=CA-4 SWSI ARR 1 CW DBD CLASS 2; O=11/16"; O/2=11/32"; P=7 7/16"; R=14 7/8"; S=10"
- 165_CA-4_SWSI_ARR_1_CW_DBD_CLASS_3: ((D-B)/2)-.125"=1 7/8"; ((K-B)/2)+B=15 31/32"; (D-B)/2=2"; (R-B)/2=1 1/8"; -(((D - B) / 2) - 1/8")=-1 7/8"; -(((K-B)/2)+L)=-7 11/32"; -(((K-B)/2)-.125")=-3 7/32"; -(ARR_2_L - ARR_2_K)=-17 5/8"; -ARR_1_J=-1 7/16"; 2ARR_1_J=2 7/8"; 2ARR_1_J+1"=3 7/8"; A=18 1/16"; ARR_1_G=11 11/16"; ARR_1_H=10 15/16"; ARR_1_J=1 7/16"; ARR_1_J/2=23/32"; ARR_1_K=34 1/4"; ARR_1_K-D=17 5/8"; ARR_1_M=1"; ARR_1_N=15 1/8"; ARR_1_U=38 1/4"; ARR_1_U-D=21 5/8"; ARR_1_V=4"; ARR_2_K=4"; ARR_2_L=21 5/8"; ARR_2_L-ARR_2_K=17 5/8"; B=12 5/8"; D=16 5/8"; D-((D-B)/2)=14 5/8"; E=14 3/8"; E+(INLET_RAD+1.5")=26 3/8"; E-(INLET_RAD+1.5")=2 1/8"; F=34 3/8"; F-E=20"; F/5=6 7/8"; G=30 7/8"; H=14 1/4"; INLET_DIA=21 1/4"; INLET_RAD=10 5/8"; INLET_RAD+1.5"=12 1/8"; INLET_RAD/2=5 5/16"; J=2"; K=19 5/16"; L=4"; M=23 15/16"; MOTOR_RAD=4 5/16"; Model=CA-4 SWSI ARR 1 CW DBD CLASS 3; O=11/16"; O/2=11/32"; P=7 7/16"; R=14 7/8"; S=10"
- 180_CA-4_SWSI_ARR_1_CW_DBD_CLASS_2: ((D-B)/2)-.125"=1 7/8"; ((K-B)/2)+B=17 3/32"; (D-B)/2=2"; (R-B)/2=1 1/8"; -(((D - B) / 2) - 1/8")=-1 7/8"; -(((K-B)/2)+L)=-7 27/32"; -(((K-B)/2)-.125")=-3 7/32"; -(ARR_2_L - ARR_2_K)=-20 1/8"; -ARR_1_J=-1 7/16"; 2ARR_1_J=2 7/8"; 2ARR_1_J+1"=3 7/8"; A=19 11/16"; ARR_1_G=12 7/16"; ARR_1_H=11 11/16"; ARR_1_J=1 7/16"; ARR_1_J/2=23/32"; ARR_1_K=37 7/8"; ARR_1_K-D=20 1/8"; ARR_1_M=1"; ARR_1_N=17 5/8"; ARR_1_U=42 1/8"; ARR_1_U-D=24 3/8"; ARR_1_V=4 1/4"; ARR_2_K=4 1/4"; ARR_2_L=24 3/8"; ARR_2_L-ARR_2_K=20 1/8"; B=13 3/4"; D=17 3/4"; D-((D-B)/2)=15 3/4"; E=15 5/8"; E+(INLET_RAD+1.5")=28 3/8"; E-(INLET_RAD+1.5")=2 5/8"; F=37 1/8"; F-E=21 1/2"; F/5=7 7/16"; G=33 5/8"; H=15 1/2"; INLET_DIA=22 3/4"; INLET_RAD=11 3/8"; INLET_RAD+1.5"=12 7/8"; INLET_RAD/2=5 11/16"; J=2"; K=20 7/16"; L=4 1/2"; M=24 15/16"; MOTOR_RAD=4 5/16"; Model=CA-4 SWSI ARR 1 CW DBD CLASS 2; O=11/16"; O/2=11/32"; P=8"; R=16"; S=11"
- 180_CA-4_SWSI_ARR_1_CW_DBD_CLASS_3: ((D-B)/2)-.125"=1 7/8"; ((K-B)/2)+B=17 3/32"; (D-B)/2=2"; (R-B)/2=1 1/8"; -(((D - B) / 2) - 1/8")=-1 7/8"; -(((K-B)/2)+L)=-7 27/32"; -(((K-B)/2)-.125")=-3 7/32"; -(ARR_2_L - ARR_2_K)=-20 1/8"; -ARR_1_J=-1 11/16"; 2ARR_1_J=3 3/8"; 2ARR_1_J+1"=4 3/8"; A=19 11/16"; ARR_1_G=12 7/16"; ARR_1_H=11 11/16"; ARR_1_J=1 11/16"; ARR_1_J/2=27/32"; ARR_1_K=37 7/8"; ARR_1_K-D=20 1/8"; ARR_1_M=1"; ARR_1_N=17 5/8"; ARR_1_U=42 1/8"; ARR_1_U-D=24 3/8"; ARR_1_V=4 1/4"; ARR_2_K=4 1/4"; ARR_2_L=24 3/8"; ARR_2_L-ARR_2_K=20 1/8"; B=13 3/4"; D=17 3/4"; D-((D-B)/2)=15 3/4"; E=15 5/8"; E+(INLET_RAD+1.5")=28 3/8"; E-(INLET_RAD+1.5")=2 5/8"; F=37 1/8"; F-E=21 1/2"; F/5=7 7/16"; G=33 5/8"; H=15 1/2"; INLET_DIA=22 3/4"; INLET_RAD=11 3/8"; INLET_RAD+1.5"=12 7/8"; INLET_RAD/2=5 11/16"; J=2"; K=20 7/16"; L=4 1/2"; M=24 15/16"; MOTOR_RAD=5 1/16"; Model=CA-4 SWSI ARR 1 CW DBD CLASS 3; O=11/16"; O/2=11/32"; P=8"; R=16"; S=11"
- 195_CA-4_SWSI_ARR_1_CW_DBD_CLASS_2: ((D-B)/2)-.125"=1 7/8"; ((K-B)/2)+B=18 13/16"; (D-B)/2=2"; (R-B)/2=1 1/8"; -(((D - B) / 2) - 1/8")=-1 7/8"; -(((K-B)/2)+L)=-8 3/8"; -(((K-B)/2)-.125")=-3 3/4"; -(ARR_2_L - ARR_2_K)=-20 1/8"; -ARR_1_J=-1 7/16"; 2ARR_1_J=2 7/8"; 2ARR_1_J+1"=3 7/8"; A=21 5/16"; ARR_1_G=13 3/16"; ARR_1_H=12 7/16"; ARR_1_J=1 7/16"; ARR_1_J/2=23/32"; ARR_1_K=39 1/16"; ARR_1_K-D=20 1/8"; ARR_1_M=1"; ARR_1_N=17 5/8"; ARR_1_U=43 5/16"; ARR_1_U-D=24 3/8"; ARR_1_V=4 1/4"; ARR_2_K=4 1/4"; ARR_2_L=24 3/8"; ARR_2_L-ARR_2_K=20 1/8"; B=14 15/16"; D=18 15/16"; D-((D-B)/2)=16 15/16"; E=16 3/4"; E+(INLET_RAD+1.5")=30 3/8"; E-(INLET_RAD+1.5")=3 1/8"; F=40"; F-E=23 1/4"; F/5=8"; G=36 1/4"; H=16 3/4"; INLET_DIA=24 1/4"; INLET_RAD=12 1/8"; INLET_RAD+1.5"=13 5/8"; INLET_RAD/2=6 1/16"; J=2"; K=22 11/16"; L=4 1/2"; M=27 3/16"; MOTOR_RAD=4 5/16"; Model=CA-4 SWSI ARR 1 CW DBD CLASS 2; O=11/16"; O/2=11/32"; P=8 19/32"; R=17 3/16"; S=11 1/2"
- 195_CA-4_SWSI_ARR_1_CW_DBD_CLASS_3: ((D-B)/2)-.125"=1 7/8"; ((K-B)/2)+B=18 13/16"; (D-B)/2=2"; (R-B)/2=1 1/8"; -(((D - B) / 2) - 1/8")=-1 7/8"; -(((K-B)/2)+L)=-8 3/8"; -(((K-B)/2)-.125")=-3 3/4"; -(ARR_2_L - ARR_2_K)=-20 1/8"; -ARR_1_J=-1 11/16"; 2ARR_1_J=3 3/8"; 2ARR_1_J+1"=4 3/8"; A=21 5/16"; ARR_1_G=13 3/16"; ARR_1_H=12 7/16"; ARR_1_J=1 11/16"; ARR_1_J/2=27/32"; ARR_1_K=39 1/16"; ARR_1_K-D=20 1/8"; ARR_1_M=1"; ARR_1_N=17 5/8"; ARR_1_U=43 5/16"; ARR_1_U-D=24 3/8"; ARR_1_V=4 1/4"; ARR_2_K=4 1/4"; ARR_2_L=24 3/8"; ARR_2_L-ARR_2_K=20 1/8"; B=14 15/16"; D=18 15/16"; D-((D-B)/2)=16 15/16"; E=16 3/4"; E+(INLET_RAD+1.5")=30 3/8"; E-(INLET_RAD+1.5")=3 1/8"; F=40"; F-E=23 1/4"; F/5=8"; G=36 1/4"; H=16 3/4"; INLET_DIA=24 1/4"; INLET_RAD=12 1/8"; INLET_RAD+1.5"=13 5/8"; INLET_RAD/2=6 1/16"; J=2"; K=22 11/16"; L=4 1/2"; M=27 3/16"; MOTOR_RAD=5 1/16"; Model=CA-4 SWSI ARR 1 CW DBD CLASS 3; O=11/16"; O/2=11/32"; P=8 19/32"; R=17 3/16"; S=11 1/2"
- 210_CA-4_SWSI_ARR_1_CW_DBD_CLASS_3: ((D-B)/2)-.125"=1 7/8"; ((K-B)/2)+B=19 15/16"; (D-B)/2=2"; (R-B)/2=1 1/8"; -(((D - B) / 2) - 1/8")=-1 7/8"; -(((K-B)/2)+L)=-8 7/8"; -(((K-B)/2)-.125")=-3 3/4"; -(ARR_2_L - ARR_2_K)=-23 1/8"; -ARR_1_J=-1 15/16"; 2ARR_1_J=3 7/8"; 2ARR_1_J+1"=4 7/8"; A=23"; ARR_1_G=14 1/16"; ARR_1_H=13 5/16"; ARR_1_J=1 15/16"; ARR_1_J/2=31/32"; ARR_1_K=42 3/16"; ARR_1_K-D=22 1/8"; ARR_1_M=1"; ARR_1_N=19 9/16"; ARR_1_U=46 7/16"; ARR_1_U-D=26 3/8"; ARR_1_V=4 1/4"; ARR_2_K=4 1/4"; ARR_2_L=27 3/8"; ARR_2_L-ARR_2_K=23 1/8"; B=16 1/16"; D=20 1/16"; D-((D-B)/2)=18 1/16"; E=18"; E+(INLET_RAD+1.5")=32 5/8"; E-(INLET_RAD+1.5")=3 5/8"; F=42 7/8"; F-E=24 7/8"; F/5=8 9/16"; G=39 1/8"; H=18 1/8"; INLET_DIA=26"; INLET_RAD=13"; INLET_RAD+1.5"=14 1/2"; INLET_RAD/2=6 1/2"; J=2"; K=23 13/16"; L=5"; M=28 13/16"; MOTOR_RAD=5 13/16"; Model=CA-4 SWSI ARR 1 CW DBD CLASS 3; O=13/16"; O/2=13/32"; P=9 5/32"; R=18 5/16"; S=12"
- 210_CA-4_SWSI_ARR_1_CW_DBD_CLASS_2: ((D-B)/2)-.125"=1 7/8"; ((K-B)/2)+B=19 15/16"; (D-B)/2=2"; (R-B)/2=1 1/8"; -(((D - B) / 2) - 1/8")=-1 7/8"; -(((K-B)/2)+L)=-8 7/8"; -(((K-B)/2)-.125")=-3 3/4"; -(ARR_2_L - ARR_2_K)=-23 1/8"; -ARR_1_J=-1 11/16"; 2ARR_1_J=3 3/8"; 2ARR_1_J+1"=4 3/8"; A=23"; ARR_1_G=14 1/16"; ARR_1_H=13 5/16"; ARR_1_J=1 11/16"; ARR_1_J/2=27/32"; ARR_1_K=42 3/16"; ARR_1_K-D=22 1/8"; ARR_1_M=1"; ARR_1_N=19 9/16"; ARR_1_U=46 7/16"; ARR_1_U-D=26 3/8"; ARR_1_V=4 1/4"; ARR_2_K=4 1/4"; ARR_2_L=27 3/8"; ARR_2_L-ARR_2_K=23 1/8"; B=16 1/16"; D=20 1/16"; D-((D-B)/2)=18 1/16"; E=18"; E+(INLET_RAD+1.5")=32 5/8"; E-(INLET_RAD+1.5")=3 5/8"; F=42 7/8"; F-E=24 7/8"; F/5=8 9/16"; G=39 1/8"; H=18 1/8"; INLET_DIA=26"; INLET_RAD=13"; INLET_RAD+1.5"=14 1/2"; INLET_RAD/2=6 1/2"; J=2"; K=23 13/16"; L=5"; M=28 13/16"; MOTOR_RAD=5 1/16"; Model=CA-4 SWSI ARR 1 CW DBD CLASS 2; O=13/16"; O/2=13/32"; P=9 5/32"; R=18 5/16"; S=12"
- 225_CA-4_SWSI_ARR_1_CW_DBD_CLASS_2: ((D-B)/2)-.125"=1 7/8"; ((K-B)/2)+B=21 1/16"; (D-B)/2=2"; (R-B)/2=1 1/8"; -(((D - B) / 2) - 1/8")=-1 7/8"; -(((K-B)/2)+L)=-8 7/8"; -(((K-B)/2)-.125")=-3 3/4"; -(ARR_2_L - ARR_2_K)=-23 1/8"; -ARR_1_J=-1 11/16"; 2ARR_1_J=3 3/8"; 2ARR_1_J+1"=4 3/8"; A=24 5/8"; ARR_1_G=14 13/16"; ARR_1_H=14 1/16"; ARR_1_J=1 11/16"; ARR_1_J/2=27/32"; ARR_1_K=43 5/16"; ARR_1_K-D=22 1/8"; ARR_1_M=1"; ARR_1_N=19 9/16"; ARR_1_U=47 9/16"; ARR_1_U-D=26 3/8"; ARR_1_V=4 1/4"; ARR_2_K=4 1/4"; ARR_2_L=27 3/8"; ARR_2_L-ARR_2_K=23 1/8"; B=17 3/16"; D=21 3/16"; D-((D-B)/2)=19 3/16"; E=19 1/4"; E+(INLET_RAD+1.5")=34 5/8"; E-(INLET_RAD+1.5")=4 1/8"; F=45 3/4"; F-E=26 1/2"; F/5=9 5/32"; G=41 3/4"; H=19 3/8"; INLET_DIA=27 1/2"; INLET_RAD=13 3/4"; INLET_RAD+1.5"=15 1/4"; INLET_RAD/2=6 7/8"; J=2"; K=24 15/16"; L=5"; M=29 15/16"; MOTOR_RAD=5 1/16"; Model=CA-4 SWSI ARR 1 CW DBD CLASS 2; O=13/16"; O/2=13/32"; P=9 23/32"; R=19 7/16"; S=12 1/2"
- 225_CA-4_SWSI_ARR_1_CW_DBD_CLASS_3: ((D-B)/2)-.125"=1 7/8"; ((K-B)/2)+B=21 1/16"; (D-B)/2=2"; (R-B)/2=1 1/8"; -(((D - B) / 2) - 1/8")=-1 7/8"; -(((K-B)/2)+L)=-8 7/8"; -(((K-B)/2)-.125")=-3 3/4"; -(ARR_2_L - ARR_2_K)=-23 1/8"; -ARR_1_J=-1 15/16"; 2ARR_1_J=3 7/8"; 2ARR_1_J+1"=4 7/8"; A=24 5/8"; ARR_1_G=14 13/16"; ARR_1_H=14 1/16"; ARR_1_J=1 15/16"; ARR_1_J/2=31/32"; ARR_1_K=43 5/16"; ARR_1_K-D=22 1/8"; ARR_1_M=1"; ARR_1_N=19 9/16"; ARR_1_U=47 9/16"; ARR_1_U-D=26 3/8"; ARR_1_V=4 1/4"; ARR_2_K=4 1/4"; ARR_2_L=27 3/8"; ARR_2_L-ARR_2_K=23 1/8"; B=17 3/16"; D=21 3/16"; D-((D-B)/2)=19 3/16"; E=19 1/4"; E+(INLET_RAD+1.5")=34 5/8"; E-(INLET_RAD+1.5")=4 1/8"; F=45 3/4"; F-E=26 1/2"; F/5=9 5/32"; G=41 3/4"; H=19 3/8"; INLET_DIA=27 1/2"; INLET_RAD=13 3/4"; INLET_RAD+1.5"=15 1/4"; INLET_RAD/2=6 7/8"; J=2"; K=24 15/16"; L=5"; M=29 15/16"; MOTOR_RAD=5 13/16"; Model=CA-4 SWSI ARR 1 CW DBD CLASS 3; O=13/16"; O/2=13/32"; P=9 23/32"; R=19 7/16"; S=12 1/2"
- 245_CA-4_SWSI_ARR_1_CW_DBD_CLASS_2: ((D-B)/2)-.125"=1 7/8"; ((K-B)/2)+B=22 5/8"; (D-B)/2=2"; (R-B)/2=1 1/8"; -(((D - B) / 2) - 1/8")=-1 7/8"; -(((K-B)/2)+L)=-9 3/8"; -(((K-B)/2)-.125")=-3 3/4"; -(ARR_2_L - ARR_2_K)=-22 9/16"; -ARR_1_J=-1 15/16"; 2ARR_1_J=3 7/8"; 2ARR_1_J+1"=4 7/8"; A=26 13/16"; ARR_1_G=15 13/16"; ARR_1_H=15 1/16"; ARR_1_J=1 15/16"; ARR_1_J/2=31/32"; ARR_1_K=45 3/8"; ARR_1_K-D=22 5/8"; ARR_1_M=1"; ARR_1_N=20 1/8"; ARR_1_U=50 9/16"; ARR_1_U-D=27 13/16"; ARR_1_V=5 1/4"; ARR_2_K=5 1/4"; ARR_2_L=27 13/16"; ARR_2_L-ARR_2_K=22 9/16"; B=18 3/4"; D=22 3/4"; D-((D-B)/2)=20 3/4"; E=20 7/8"; E+(INLET_RAD+1.5")=37 3/8"; E-(INLET_RAD+1.5")=4 7/8"; F=49 1/2"; F-E=28 5/8"; F/5=9 29/32"; G=45 3/8"; H=21 1/8"; INLET_DIA=29 1/2"; INLET_RAD=14 3/4"; INLET_RAD+1.5"=16 1/4"; INLET_RAD/2=7 3/8"; J=2"; K=26 1/2"; L=5 1/2"; M=32"; MOTOR_RAD=5 13/16"; Model=CA-4 SWSI ARR 1 CW DBD CLASS 2; O=13/16"; O/2=13/32"; P=10 1/2"; R=21"; S=13 1/2"
- 245_CA-4_SWSI_ARR_1_CW_DBD_CLASS_3: ((D-B)/2)-.125"=1 7/8"; ((K-B)/2)+B=22 5/8"; (D-B)/2=2"; (R-B)/2=1 1/8"; -(((D - B) / 2) - 1/8")=-1 7/8"; -(((K-B)/2)+L)=-9 3/8"; -(((K-B)/2)-.125")=-3 3/4"; -(ARR_2_L - ARR_2_K)=-22 9/16"; -ARR_1_J=-2 7/16"; 2ARR_1_J=4 7/8"; 2ARR_1_J+1"=5 7/8"; A=26 13/16"; ARR_1_G=15 13/16"; ARR_1_H=15 1/16"; ARR_1_J=2 7/16"; ARR_1_J/2=1 7/32"; ARR_1_K=45 3/8"; ARR_1_K-D=22 5/8"; ARR_1_M=1"; ARR_1_N=20 1/8"; ARR_1_U=50 9/16"; ARR_1_U-D=27 13/16"; ARR_1_V=5 1/4"; ARR_2_K=5 1/4"; ARR_2_L=27 13/16"; ARR_2_L-ARR_2_K=22 9/16"; B=18 3/4"; D=22 3/4"; D-((D-B)/2)=20 3/4"; E=20 7/8"; E+(INLET_RAD+1.5")=37 3/8"; E-(INLET_RAD+1.5")=4 7/8"; F=49 1/2"; F-E=28 5/8"; F/5=9 29/32"; G=45 3/8"; H=21 1/8"; INLET_DIA=29 1/2"; INLET_RAD=14 3/4"; INLET_RAD+1.5"=16 1/4"; INLET_RAD/2=7 3/8"; J=2"; K=26 1/2"; L=5 1/2"; M=32"; MOTOR_RAD=7 5/16"; Model=CA-4 SWSI ARR 1 CW DBD CLASS 3; O=13/16"; O/2=13/32"; P=10 1/2"; R=21"; S=13 1/2"
- 270_CA-4_SWSI_ARR_1_CW_DBD_CLASS_2: ((D-B)/2)-.125"=1 7/8"; ((K-B)/2)+B=24 1/2"; (D-B)/2=2"; (R-B)/2=1 1/8"; -(((D - B) / 2) - 1/8")=-1 7/8"; -(((K-B)/2)+L)=-9 7/8"; -(((K-B)/2)-.125")=-3 3/4"; -(ARR_2_L - ARR_2_K)=-22 9/16"; -ARR_1_J=-1 15/16"; 2ARR_1_J=3 7/8"; 2ARR_1_J+1"=4 7/8"; A=29 9/16"; ARR_1_G=17 3/16"; ARR_1_H=16 7/16"; ARR_1_J=1 15/16"; ARR_1_J/2=31/32"; ARR_1_K=47 1/4"; ARR_1_K-D=22 5/8"; ARR_1_M=1"; ARR_1_N=20 1/8"; ARR_1_U=52 7/16"; ARR_1_U-D=27 13/16"; ARR_1_V=5 1/4"; ARR_2_K=5 1/4"; ARR_2_L=27 13/16"; ARR_2_L-ARR_2_K=22 9/16"; B=20 5/8"; D=24 5/8"; D-((D-B)/2)=22 5/8"; E=23 3/8"; E+(INLET_RAD+1.5")=40 3/4"; E-(INLET_RAD+1.5")=5 3/4"; F=54 3/4"; F-E=31 3/8"; F/5=10 15/16"; G=49 7/8"; H=23 1/4"; INLET_DIA=32"; INLET_RAD=16"; INLET_RAD+1.5"=17 1/2"; INLET_RAD/2=8"; J=2"; K=28 3/8"; L=6"; M=34 3/8"; MOTOR_RAD=5 13/16"; Model=CA-4 SWSI ARR 1 CW DBD CLASS 2; O=13/16"; O/2=13/32"; P=11 7/16"; R=22 7/8"; S=15"
- 270_CA-4_SWSI_ARR_1_CW_DBD_CLASS_3: ((D-B)/2)-.125"=1 7/8"; ((K-B)/2)+B=24 1/2"; (D-B)/2=2"; (R-B)/2=1 1/8"; -(((D - B) / 2) - 1/8")=-1 7/8"; -(((K-B)/2)+L)=-9 7/8"; -(((K-B)/2)-.125")=-3 3/4"; -(ARR_2_L - ARR_2_K)=-22 9/16"; -ARR_1_J=-2 3/16"; 2ARR_1_J=4 3/8"; 2ARR_1_J+1"=5 3/8"; A=29 9/16"; ARR_1_G=17 3/16"; ARR_1_H=16 7/16"; ARR_1_J=2 3/16"; ARR_1_J/2=1 3/32"; ARR_1_K=47 1/4"; ARR_1_K-D=22 5/8"; ARR_1_M=1"; ARR_1_N=20 1/8"; ARR_1_U=52 7/16"; ARR_1_U-D=27 13/16"; ARR_1_V=5 1/4"; ARR_2_K=5 1/4"; ARR_2_L=27 13/16"; ARR_2_L-ARR_2_K=22 9/16"; B=20 5/8"; D=24 5/8"; D-((D-B)/2)=22 5/8"; E=23 3/8"; E+(INLET_RAD+1.5")=40 3/4"; E-(INLET_RAD+1.5")=5 3/4"; F=54 3/4"; F-E=31 3/8"; F/5=10 15/16"; G=49 7/8"; H=23 1/4"; INLET_DIA=32"; INLET_RAD=16"; INLET_RAD+1.5"=17 1/2"; INLET_RAD/2=8"; J=2"; K=28 3/8"; L=6"; M=34 3/8"; MOTOR_RAD=6 9/16"; Model=CA-4 SWSI ARR 1 CW DBD CLASS 3; O=13/16"; O/2=13/32"; P=11 7/16"; R=22 7/8"; S=15"
- 300_CA-4_SWSI_ARR_1_CW_DBD_CLASS_2: ((D-B)/2)-.125"=1 7/8"; ((K-B)/2)+B=26 13/16"; (D-B)/2=2"; (R-B)/2=1 1/8"; -(((D - B) / 2) - 1/8")=-1 7/8"; -(((K-B)/2)+L)=-10 3/8"; -(((K-B)/2)-.125")=-3 3/4"; -(ARR_2_L - ARR_2_K)=-24 7/8"; -ARR_1_J=-2 3/16"; 2ARR_1_J=4 3/8"; 2ARR_1_J+1"=5 3/8"; A=32 13/16"; ARR_1_G=18 11/16"; ARR_1_H=17 15/16"; ARR_1_J=2 3/16"; ARR_1_J/2=1 3/32"; ARR_1_K=51 13/16"; ARR_1_K-D=24 7/8"; ARR_1_M=1"; ARR_1_N=22 3/8"; ARR_1_U=57 11/16"; ARR_1_U-D=30 3/4"; ARR_1_V=5 7/8"; ARR_2_K=5 7/8"; ARR_2_L=30 3/4"; ARR_2_L-ARR_2_K=24 7/8"; B=22 15/16"; D=26 15/16"; D-((D-B)/2)=24 15/16"; E=25 3/8"; E+(INLET_RAD+1.5")=44 7/8"; E-(INLET_RAD+1.5")=6 7/8"; F=60"; F-E=34 5/8"; F/5=12"; G=55 3/8"; H=25 7/8"; INLET_DIA=35"; INLET_RAD=17 1/2"; INLET_RAD+1.5"=19"; INLET_RAD/2=8 3/4"; J=2"; K=30 11/16"; L=6 1/2"; M=37 3/16"; MOTOR_RAD=6 9/16"; Model=CA-4 SWSI ARR 1 CW DBD CLASS 2; O=13/16"; O/2=13/32"; P=12 19/32"; R=25 3/16"; S=16 1/2"
- 300_CA-4_SWSI_ARR_1_CW_DBD_CLASS_3: ((D-B)/2)-.125"=1 7/8"; ((K-B)/2)+B=26 13/16"; (D-B)/2=2"; (R-B)/2=1 1/8"; -(((D - B) / 2) - 1/8")=-1 7/8"; -(((K-B)/2)+L)=-10 3/8"; -(((K-B)/2)-.125")=-3 3/4"; -(ARR_2_L - ARR_2_K)=-24 7/8"; -ARR_1_J=-2 7/16"; 2ARR_1_J=4 7/8"; 2ARR_1_J+1"=5 7/8"; A=32 13/16"; ARR_1_G=18 11/16"; ARR_1_H=17 15/16"; ARR_1_J=2 7/16"; ARR_1_J/2=1 7/32"; ARR_1_K=51 13/16"; ARR_1_K-D=24 7/8"; ARR_1_M=1"; ARR_1_N=22 3/8"; ARR_1_U=57 11/16"; ARR_1_U-D=30 3/4"; ARR_1_V=5 7/8"; ARR_2_K=5 7/8"; ARR_2_L=30 3/4"; ARR_2_L-ARR_2_K=24 7/8"; B=22 15/16"; D=26 15/16"; D-((D-B)/2)=24 15/16"; E=25 3/8"; E+(INLET_RAD+1.5")=44 7/8"; E-(INLET_RAD+1.5")=6 7/8"; F=60"; F-E=34 5/8"; F/5=12"; G=55 3/8"; H=25 7/8"; INLET_DIA=35"; INLET_RAD=17 1/2"; INLET_RAD+1.5"=19"; INLET_RAD/2=8 3/4"; J=2"; K=30 11/16"; L=6 1/2"; M=37 3/16"; MOTOR_RAD=7 5/16"; Model=CA-4 SWSI ARR 1 CW DBD CLASS 3; O=13/16"; O/2=13/32"; P=12 19/32"; R=25 3/16"; S=16 1/2"
- 330_CA-4_SWSI_ARR_1_CW_DBD_CLASS_2: ((D-B)/2)-.125"=1 7/8"; ((K-B)/2)+B=29 1/8"; (D-B)/2=2"; (R-B)/2=1 1/8"; -(((D - B) / 2) - 1/8")=-1 7/8"; -(((K-B)/2)+L)=-10 7/8"; -(((K-B)/2)-.125")=-3 3/4"; -(ARR_2_L - ARR_2_K)=-24 7/8"; -ARR_1_J=-2 3/16"; 2ARR_1_J=4 3/8"; 2ARR_1_J+1"=5 3/8"; A=36 1/8"; ARR_1_G=20 3/16"; ARR_1_H=19 7/16"; ARR_1_J=2 3/16"; ARR_1_J/2=1 3/32"; ARR_1_K=54 1/8"; ARR_1_K-D=24 7/8"; ARR_1_M=1"; ARR_1_N=22 3/8"; ARR_1_U=60"; ARR_1_U-D=30 3/4"; ARR_1_V=5 7/8"; ARR_2_K=5 7/8"; ARR_2_L=30 3/4"; ARR_2_L-ARR_2_K=24 7/8"; B=25 1/4"; D=29 1/4"; D-((D-B)/2)=27 1/4"; E=27 7/8"; E+(INLET_RAD+1.5")=48 7/8"; E-(INLET_RAD+1.5")=7 7/8"; F=65 3/4"; F-E=37 7/8"; F/5=13 5/32"; G=60 3/4"; H=28 3/8"; INLET_DIA=38"; INLET_RAD=19"; INLET_RAD+1.5"=20 1/2"; INLET_RAD/2=9 1/2"; J=2"; K=33"; L=7"; M=40"; MOTOR_RAD=6 9/16"; Model=CA-4 SWSI ARR 1 CW DBD CLASS 2; O=13/16"; O/2=13/32"; P=13 3/4"; R=27 1/2"; S=18"
- 330_CA-4_SWSI_ARR_1_CW_DBD_CLASS_3: ((D-B)/2)-.125"=1 7/8"; ((K-B)/2)+B=29 1/8"; (D-B)/2=2"; (R-B)/2=1 1/8"; -(((D - B) / 2) - 1/8")=-1 7/8"; -(((K-B)/2)+L)=-10 7/8"; -(((K-B)/2)-.125")=-3 3/4"; -(ARR_2_L - ARR_2_K)=-24 7/8"; -ARR_1_J=-2 7/16"; 2ARR_1_J=4 7/8"; 2ARR_1_J+1"=5 7/8"; A=36 1/8"; ARR_1_G=20 3/16"; ARR_1_H=19 7/16"; ARR_1_J=2 7/16"; ARR_1_J/2=1 7/32"; ARR_1_K=54 1/8"; ARR_1_K-D=24 7/8"; ARR_1_M=1"; ARR_1_N=22 3/8"; ARR_1_U=60"; ARR_1_U-D=30 3/4"; ARR_1_V=5 7/8"; ARR_2_K=5 7/8"; ARR_2_L=30 3/4"; ARR_2_L-ARR_2_K=24 7/8"; B=25 1/4"; D=29 1/4"; D-((D-B)/2)=27 1/4"; E=27 7/8"; E+(INLET_RAD+1.5")=48 7/8"; E-(INLET_RAD+1.5")=7 7/8"; F=65 3/4"; F-E=37 7/8"; F/5=13 5/32"; G=60 3/4"; H=28 3/8"; INLET_DIA=38"; INLET_RAD=19"; INLET_RAD+1.5"=20 1/2"; INLET_RAD/2=9 1/2"; J=2"; K=33"; L=7"; M=40"; MOTOR_RAD=7 5/16"; Model=CA-4 SWSI ARR 1 CW DBD CLASS 3; O=13/16"; O/2=13/32"; P=13 3/4"; R=27 1/2"; S=18"
- 365_CA-4_SWSI_ARR_1_CW_DBD_CLASS_2: ((D-B)/2)-.125"=1 7/8"; ((K-B)/2)+B=31 3/4"; (D-B)/2=2"; (R-B)/2=1 1/8"; -(((D - B) / 2) - 1/8")=-1 7/8"; -(((K-B)/2)+L)=-11 3/8"; -(((K-B)/2)-.125")=-3 3/4"; -(ARR_2_L - ARR_2_K)=-27 1/8"; -ARR_1_J=-2 7/16"; 2ARR_1_J=4 7/8"; 2ARR_1_J+1"=5 7/8"; A=39 15/16"; ARR_1_G=22 7/16"; ARR_1_H=21 11/16"; ARR_1_J=2 7/16"; ARR_1_J/2=1 7/32"; ARR_1_K=59"; ARR_1_K-D=27 1/8"; ARR_1_M=1"; ARR_1_N=24 5/8"; ARR_1_U=64 7/8"; ARR_1_U-D=33"; ARR_1_V=5 7/8"; ARR_2_K=5 7/8"; ARR_2_L=33"; ARR_2_L-ARR_2_K=27 1/8"; B=27 7/8"; D=31 7/8"; D-((D-B)/2)=29 7/8"; E=30 5/8"; E+(INLET_RAD+1.5")=53 5/8"; E-(INLET_RAD+1.5")=9 1/8"; F=72 3/8"; F-E=41 3/4"; F/5=14 15/32"; G=67"; H=31 3/8"; INLET_DIA=41 1/2"; INLET_RAD=20 3/4"; INLET_RAD+1.5"=22 1/4"; INLET_RAD/2=10 3/8"; J=2"; K=35 5/8"; L=7 1/2"; M=43 1/8"; MOTOR_RAD=7 5/16"; Model=CA-4 SWSI ARR 1 CW DBD CLASS 2; O=13/16"; O/2=13/32"; P=15 1/16"; R=30 1/8"; S=20"
- 365_CA-4_SWSI_ARR_1_CW_DBD_CLASS_3: ((D-B)/2)-.125"=1 7/8"; ((K-B)/2)+B=31 3/4"; (D-B)/2=2"; (R-B)/2=1 1/8"; -(((D - B) / 2) - 1/8")=-1 7/8"; -(((K-B)/2)+L)=-11 3/8"; -(((K-B)/2)-.125")=-3 3/4"; -(ARR_2_L - ARR_2_K)=-27 1/8"; -ARR_1_J=-2 15/16"; 2ARR_1_J=5 7/8"; 2ARR_1_J+1"=6 7/8"; A=39 15/16"; ARR_1_G=22 7/16"; ARR_1_H=21 11/16"; ARR_1_J=2 15/16"; ARR_1_J/2=1 15/32"; ARR_1_K=59"; ARR_1_K-D=27 1/8"; ARR_1_M=1"; ARR_1_N=24 5/8"; ARR_1_U=64 7/8"; ARR_1_U-D=33"; ARR_1_V=5 7/8"; ARR_2_K=5 7/8"; ARR_2_L=33"; ARR_2_L-ARR_2_K=27 1/8"; B=27 7/8"; D=31 7/8"; D-((D-B)/2)=29 7/8"; E=30 5/8"; E+(INLET_RAD+1.5")=53 5/8"; E-(INLET_RAD+1.5")=9 1/8"; F=72 3/8"; F-E=41 3/4"; F/5=14 15/32"; G=67"; H=31 3/8"; INLET_DIA=41 1/2"; INLET_RAD=20 3/4"; INLET_RAD+1.5"=22 1/4"; INLET_RAD/2=10 3/8"; J=2"; K=35 5/8"; L=7 1/2"; M=43 1/8"; MOTOR_RAD=8 13/16"; Model=CA-4 SWSI ARR 1 CW DBD CLASS 3; O=13/16"; O/2=13/32"; P=15 1/16"; R=30 1/8"; S=20"
- 402_CA-4_SWSI_ARR_1_CW_DBD_CLASS_2: ((D-B)/2)-.125"=2 7/8"; ((K-B)/2)+B=34 11/16"; (D-B)/2=3"; (R-B)/2=1 3/4"; -(((D - B) / 2) - 1/8")=-2 7/8"; -(((K-B)/2)+L)=-11 15/16"; -(((K-B)/2)-.125")=-3 13/16"; -(ARR_2_L - ARR_2_K)=-25 7/16"; -ARR_1_J=-2 7/16"; 2ARR_1_J=4 7/8"; 2ARR_1_J+1"=5 7/8"; A=44 1/16"; ARR_1_G=24 3/8"; ARR_1_H=22 3/8"; ARR_1_J=2 7/16"; ARR_1_J/2=1 7/32"; ARR_1_K=62 15/16"; ARR_1_K-D=26 3/16"; ARR_1_M=1 1/4"; ARR_1_N=23 13/16"; ARR_1_U=68 1/16"; ARR_1_U-D=31 5/16"; ARR_1_V=5 7/8"; ARR_2_K=5 7/8"; ARR_2_L=31 5/16"; ARR_2_L-ARR_2_K=25 7/16"; B=30 3/4"; D=36 3/4"; D-((D-B)/2)=33 3/4"; E=33 5/8"; E+(INLET_RAD+1.5")=58 3/4"; E-(INLET_RAD+1.5")=10 1/2"; F=80 3/8"; F-E=46 3/4"; F/5=16 1/16"; G=73 7/8"; H=34 5/8"; INLET_DIA=45 1/4"; INLET_RAD=22 5/8"; INLET_RAD+1.5"=24 1/8"; INLET_RAD/2=11 5/16"; J=3"; K=38 5/8"; L=8"; M=46 5/8"; MOTOR_RAD=7 5/16"; Model=CA-4 SWSI ARR 1 CW DBD CLASS 2; O=1 1/16"; O/2=17/32"; P=17 1/8"; R=34 1/4"; S=22"
- 402_CA-4_SWSI_ARR_1_CW_DBD_CLASS_3: ((D-B)/2)-.125"=2 7/8"; ((K-B)/2)+B=34 11/16"; (D-B)/2=3"; (R-B)/2=1 3/4"; -(((D - B) / 2) - 1/8")=-2 7/8"; -(((K-B)/2)+L)=-11 15/16"; -(((K-B)/2)-.125")=-3 13/16"; -(ARR_2_L - ARR_2_K)=-25 7/16"; -ARR_1_J=-2 15/16"; 2ARR_1_J=5 7/8"; 2ARR_1_J+1"=6 7/8"; A=44 1/16"; ARR_1_G=24 3/8"; ARR_1_H=22 3/8"; ARR_1_J=2 15/16"; ARR_1_J/2=1 15/32"; ARR_1_K=62 15/16"; ARR_1_K-D=26 3/16"; ARR_1_M=1 1/4"; ARR_1_N=23 13/16"; ARR_1_U=68 1/16"; ARR_1_U-D=31 5/16"; ARR_1_V=5 7/8"; ARR_2_K=5 7/8"; ARR_2_L=31 5/16"; ARR_2_L-ARR_2_K=25 7/16"; B=30 3/4"; D=36 3/4"; D-((D-B)/2)=33 3/4"; E=33 5/8"; E+(INLET_RAD+1.5")=58 3/4"; E-(INLET_RAD+1.5")=10 1/2"; F=80 3/8"; F-E=46 3/4"; F/5=16 1/16"; G=73 7/8"; H=34 5/8"; INLET_DIA=45 1/4"; INLET_RAD=22 5/8"; INLET_RAD+1.5"=24 1/8"; INLET_RAD/2=11 5/16"; J=3"; K=38 5/8"; L=8"; M=46 5/8"; MOTOR_RAD=8 13/16"; Model=CA-4 SWSI ARR 1 CW DBD CLASS 3; O=1 1/16"; O/2=17/32"; P=17 1/8"; R=34 1/4"; S=22"
- 445_CA-4_SWSI_ARR_1_CW_DBD_CLASS_2: ((D-B)/2)-.125"=2 7/8"; ((K-B)/2)+B=37 15/16"; (D-B)/2=3"; (R-B)/2=1 3/4"; -(((D - B) / 2) - 1/8")=-2 7/8"; -(((K-B)/2)+L)=-12 7/16"; -(((K-B)/2)-.125")=-3 13/16"; -(ARR_2_L - ARR_2_K)=-26 11/16"; -ARR_1_J=-2 15/16"; 2ARR_1_J=5 7/8"; 2ARR_1_J+1"=6 7/8"; A=48 11/16"; ARR_1_G=26 1/2"; ARR_1_H=25 1/2"; ARR_1_J=2 15/16"; ARR_1_J/2=1 15/32"; ARR_1_K=66 15/16"; ARR_1_K-D=26 15/16"; ARR_1_M=1 1/4"; ARR_1_N=24 9/16"; ARR_1_U=73 1/16"; ARR_1_U-D=33 1/16"; ARR_1_V=6 3/8"; ARR_2_K=6 3/8"; ARR_2_L=33 1/16"; ARR_2_L-ARR_2_K=26 11/16"; B=34"; D=40"; D-((D-B)/2)=37"; E=37 1/8"; E+(INLET_RAD+1.5")=64 1/2"; E-(INLET_RAD+1.5")=12"; F=88 1/2"; F-E=51 3/8"; F/5=17 11/16"; G=81 1/2"; H=38 1/4"; INLET_DIA=49 1/2"; INLET_RAD=24 3/4"; INLET_RAD+1.5"=26 1/4"; INLET_RAD/2=12 3/8"; J=3"; K=41 7/8"; L=8 1/2"; M=50 3/8"; MOTOR_RAD=8 13/16"; Model=CA-4 SWSI ARR 1 CW DBD CLASS 2; O=1 1/16"; O/2=17/32"; P=18 3/4"; R=37 1/2"; S=24"
- 445_CA-4_SWSI_ARR_1_CW_DBD_CLASS_3: ((D-B)/2)-.125"=2 7/8"; ((K-B)/2)+B=37 15/16"; (D-B)/2=3"; (R-B)/2=1 3/4"; -(((D - B) / 2) - 1/8")=-2 7/8"; -(((K-B)/2)+L)=-12 7/16"; -(((K-B)/2)-.125")=-3 13/16"; -(ARR_2_L - ARR_2_K)=-26 11/16"; -ARR_1_J=-3 7/16"; 2ARR_1_J=6 7/8"; 2ARR_1_J+1"=7 7/8"; A=48 11/16"; ARR_1_G=26 1/2"; ARR_1_H=25 1/2"; ARR_1_J=3 7/16"; ARR_1_J/2=1 23/32"; ARR_1_K=66 15/16"; ARR_1_K-D=26 15/16"; ARR_1_M=1 1/4"; ARR_1_N=24 9/16"; ARR_1_U=73 1/16"; ARR_1_U-D=33 1/16"; ARR_1_V=6 3/8"; ARR_2_K=6 3/8"; ARR_2_L=33 1/16"; ARR_2_L-ARR_2_K=26 11/16"; B=34"; D=40"; D-((D-B)/2)=37"; E=37 1/8"; E+(INLET_RAD+1.5")=64 1/2"; E-(INLET_RAD+1.5")=12"; F=88 1/2"; F-E=51 3/8"; F/5=17 11/16"; G=81 1/2"; H=38 1/4"; INLET_DIA=49 1/2"; INLET_RAD=24 3/4"; INLET_RAD+1.5"=26 1/4"; INLET_RAD/2=12 3/8"; J=3"; K=41 7/8"; L=8 1/2"; M=50 3/8"; MOTOR_RAD=10 5/16"; Model=CA-4 SWSI ARR 1 CW DBD CLASS 3; O=1 1/16"; O/2=17/32"; P=18 3/4"; R=37 1/2"; S=24"
- 490_CA-4_SWSI_ARR_1_CW_DBD_CLASS_2: ((D-B)/2)-.125"=2 7/8"; ((K-B)/2)+B=41 7/8"; (D-B)/2=3"; (R-B)/2=1 3/4"; -(((D - B) / 2) - 1/8")=-2 7/8"; -(((K-B)/2)+L)=-13 7/16"; -(((K-B)/2)-.125")=-4 5/16"; -(ARR_2_L - ARR_2_K)=-26 11/16"; -ARR_1_J=-2 15/16"; 2ARR_1_J=5 7/8"; 2ARR_1_J+1"=6 7/8"; A=53 5/8"; ARR_1_G=29 1/4"; ARR_1_H=28 1/4"; ARR_1_J=2 15/16"; ARR_1_J/2=1 15/32"; ARR_1_K=70 3/8"; ARR_1_K-D=26 15/16"; ARR_1_M=1 1/4"; ARR_1_N=24 9/16"; ARR_1_U=76 1/2"; ARR_1_U-D=33 1/16"; ARR_1_V=6 3/8"; ARR_2_K=6 3/8"; ARR_2_L=33 1/16"; ARR_2_L-ARR_2_K=26 11/16"; B=37 7/16"; D=43 7/16"; D-((D-B)/2)=40 7/16"; E=40 3/4"; E+(INLET_RAD+1.5")=71 1/4"; E-(INLET_RAD+1.5")=13 1/4"; F=97"; F-E=56 1/4"; F/5=19 13/32"; G=89 3/4"; H=42 1/4"; INLET_DIA=55"; INLET_RAD=27 1/2"; INLET_RAD+1.5"=29"; INLET_RAD/2=13 3/4"; J=3"; K=46 5/16"; L=9"; M=55 5/16"; MOTOR_RAD=8 13/16"; Model=CA-4 SWSI ARR 1 CW DBD CLASS 2; O=1 1/16"; O/2=17/32"; P=20 15/32"; R=40 15/16"; S=26 1/2"
- 490_CA-4_SWSI_ARR_1_CW_DBD_CLASS_3: ((D-B)/2)-.125"=2 7/8"; ((K-B)/2)+B=41 7/8"; (D-B)/2=3"; (R-B)/2=1 3/4"; -(((D - B) / 2) - 1/8")=-2 7/8"; -(((K-B)/2)+L)=-13 7/16"; -(((K-B)/2)-.125")=-4 5/16"; -(ARR_2_L - ARR_2_K)=-26 11/16"; -ARR_1_J=-3 7/16"; 2ARR_1_J=6 7/8"; 2ARR_1_J+1"=7 7/8"; A=53 5/8"; ARR_1_G=29 1/4"; ARR_1_H=28 1/4"; ARR_1_J=3 7/16"; ARR_1_J/2=1 23/32"; ARR_1_K=70 3/8"; ARR_1_K-D=26 15/16"; ARR_1_M=1 1/4"; ARR_1_N=24 9/16"; ARR_1_U=76 1/2"; ARR_1_U-D=33 1/16"; ARR_1_V=6 3/8"; ARR_2_K=6 3/8"; ARR_2_L=33 1/16"; ARR_2_L-ARR_2_K=26 11/16"; B=37 7/16"; D=43 7/16"; D-((D-B)/2)=40 7/16"; E=40 3/4"; E+(INLET_RAD+1.5")=71 1/4"; E-(INLET_RAD+1.5")=13 1/4"; F=97"; F-E=56 1/4"; F/5=19 13/32"; G=89 3/4"; H=42 1/4"; INLET_DIA=55"; INLET_RAD=27 1/2"; INLET_RAD+1.5"=29"; INLET_RAD/2=13 3/4"; J=3"; K=46 5/16"; L=9"; M=55 5/16"; MOTOR_RAD=10 5/16"; Model=CA-4 SWSI ARR 1 CW DBD CLASS 3; O=1 1/16"; O/2=17/32"; P=20 15/32"; R=40 15/16"; S=26 1/2"
- 540_CA-4_SWSI_ARR_1_CW_DBD_CLASS_2: ((D-B)/2)-.125"=2 7/8"; ((K-B)/2)+B=46 11/16"; (D-B)/2=3"; (R-B)/2=1 3/4"; -(((D - B) / 2) - 1/8")=-2 7/8"; -(((K-B)/2)+L)=-14 15/16"; -(((K-B)/2)-.125")=-5 5/16"; -(ARR_2_L - ARR_2_K)=-26 7/8"; -ARR_1_J=-3 7/16"; 2ARR_1_J=6 7/8"; 2ARR_1_J+1"=7 7/8"; A=59 1/16"; ARR_1_G=31 3/4"; ARR_1_H=30 3/4"; ARR_1_J=3 7/16"; ARR_1_J/2=1 23/32"; ARR_1_K=74 1/4"; ARR_1_K-D=27"; ARR_1_M=1 1/4"; ARR_1_N=24 9/16"; ARR_1_U=81 5/8"; ARR_1_U-D=34 3/8"; ARR_1_V=7 1/2"; ARR_2_K=7 1/2"; ARR_2_L=34 3/8"; ARR_2_L-ARR_2_K=26 7/8"; B=41 1/4"; D=47 1/4"; D-((D-B)/2)=44 1/4"; E=44 7/8"; E+(INLET_RAD+1.5")=78"; E-(INLET_RAD+1.5")=15"; F=106 5/8"; F-E=61 3/4"; F/5=21 5/16"; G=98 3/4"; H=46 1/2"; INLET_DIA=60"; INLET_RAD=30"; INLET_RAD+1.5"=31 1/2"; INLET_RAD/2=15"; J=3"; K=52 1/8"; L=9 1/2"; M=61 5/8"; MOTOR_RAD=10 5/16"; Model=CA-4 SWSI ARR 1 CW DBD CLASS 2; O=1 1/16"; O/2=17/32"; P=22 3/8"; R=44 3/4"; S=29"
- 540_CA-4_SWSI_ARR_1_CW_DBD_CLASS_3: ((D-B)/2)-.125"=2 7/8"; ((K-B)/2)+B=46 11/16"; (D-B)/2=3"; (R-B)/2=1 3/4"; -(((D - B) / 2) - 1/8")=-2 7/8"; -(((K-B)/2)+L)=-14 15/16"; -(((K-B)/2)-.125")=-5 5/16"; -(ARR_2_L - ARR_2_K)=-26 7/8"; -ARR_1_J=-3 15/16"; 2ARR_1_J=7 7/8"; 2ARR_1_J+1"=8 7/8"; A=59 1/16"; ARR_1_G=31 3/4"; ARR_1_H=30 3/4"; ARR_1_J=3 15/16"; ARR_1_J/2=1 31/32"; ARR_1_K=74 1/4"; ARR_1_K-D=27"; ARR_1_M=1 1/4"; ARR_1_N=24 9/16"; ARR_1_U=81 5/8"; ARR_1_U-D=34 3/8"; ARR_1_V=7 1/2"; ARR_2_K=7 1/2"; ARR_2_L=34 3/8"; ARR_2_L-ARR_2_K=26 7/8"; B=41 1/4"; D=47 1/4"; D-((D-B)/2)=44 1/4"; E=44 7/8"; E+(INLET_RAD+1.5")=78"; E-(INLET_RAD+1.5")=15"; F=106 5/8"; F-E=61 3/4"; F/5=21 5/16"; G=98 3/4"; H=46 1/2"; INLET_DIA=60"; INLET_RAD=30"; INLET_RAD+1.5"=31 1/2"; INLET_RAD/2=15"; J=3"; K=52 1/8"; L=9 1/2"; M=61 5/8"; MOTOR_RAD=11 13/16"; Model=CA-4 SWSI ARR 1 CW DBD CLASS 3; O=1 1/16"; O/2=17/32"; P=22 3/8"; R=44 3/4"; S=29"
- 600_CA-4_SWSI_ARR_1_CW_DBD_CLASS_2: ((D-B)/2)-.125"=2 7/8"; ((K-B)/2)+B=51 1/4"; (D-B)/2=3"; (R-B)/2=1 3/4"; -(((D - B) / 2) - 1/8")=-2 7/8"; -(((K-B)/2)+L)=-15 7/16"; -(((K-B)/2)-.125")=-5 5/16"; -(ARR_2_L - ARR_2_K)=-26 7/8"; -ARR_1_J=-3 7/16"; 2ARR_1_J=6 7/8"; 2ARR_1_J+1"=7 7/8"; A=65 5/8"; ARR_1_G=34 3/4"; ARR_1_H=33 3/4"; ARR_1_J=3 7/16"; ARR_1_J/2=1 23/32"; ARR_1_K=78 13/16"; ARR_1_K-D=27"; ARR_1_M=1 1/4"; ARR_1_N=24 9/16"; ARR_1_U=86 3/16"; ARR_1_U-D=34 3/8"; ARR_1_V=7 1/2"; ARR_2_K=7 1/2"; ARR_2_L=34 3/8"; ARR_2_L-ARR_2_K=26 7/8"; B=45 13/16"; D=51 13/16"; D-((D-B)/2)=48 13/16"; E=49 3/4"; E+(INLET_RAD+1.5")=86 1/8"; E-(INLET_RAD+1.5")=17 1/8"; F=118"; F-E=68 1/4"; F/5=23 19/32"; G=109 5/8"; H=51 5/8"; INLET_DIA=66"; INLET_RAD=33"; INLET_RAD+1.5"=34 1/2"; INLET_RAD/2=16 1/2"; J=3"; K=56 11/16"; L=10"; M=66 11/16"; MOTOR_RAD=10 5/16"; Model=CA-4 SWSI ARR 1 CW DBD CLASS 2; O=1 1/16"; O/2=17/32"; P=24 21/32"; R=49 5/16"; S=32"
- 600_CA-4_SWSI_ARR_1_CW_DBD_CLASS_3: ((D-B)/2)-.125"=2 7/8"; ((K-B)/2)+B=51 1/4"; (D-B)/2=3"; (R-B)/2=1 3/4"; -(((D - B) / 2) - 1/8")=-2 7/8"; -(((K-B)/2)+L)=-15 7/16"; -(((K-B)/2)-.125")=-5 5/16"; -(ARR_2_L - ARR_2_K)=-26 7/8"; -ARR_1_J=-3 15/16"; 2ARR_1_J=7 7/8"; 2ARR_1_J+1"=8 7/8"; A=65 5/8"; ARR_1_G=34 3/4"; ARR_1_H=33 3/4"; ARR_1_J=3 15/16"; ARR_1_J/2=1 31/32"; ARR_1_K=78 13/16"; ARR_1_K-D=27"; ARR_1_M=1 1/4"; ARR_1_N=24 9/16"; ARR_1_U=86 3/16"; ARR_1_U-D=34 3/8"; ARR_1_V=7 1/2"; ARR_2_K=7 1/2"; ARR_2_L=34 3/8"; ARR_2_L-ARR_2_K=26 7/8"; B=45 13/16"; D=51 13/16"; D-((D-B)/2)=48 13/16"; E=49 3/4"; E+(INLET_RAD+1.5")=86 1/8"; E-(INLET_RAD+1.5")=17 1/8"; F=118"; F-E=68 1/4"; F/5=23 19/32"; G=109 5/8"; H=51 5/8"; INLET_DIA=66"; INLET_RAD=33"; INLET_RAD+1.5"=34 1/2"; INLET_RAD/2=16 1/2"; J=3"; K=56 11/16"; L=10"; M=66 11/16"; MOTOR_RAD=11 13/16"; Model=CA-4 SWSI ARR 1 CW DBD CLASS 3; O=1 1/16"; O/2=17/32"; P=24 21/32"; R=49 5/16"; S=32"

## geometry (parser evidence)
native form markers: Sweep x2
no freeform markers — native parametric forms only
